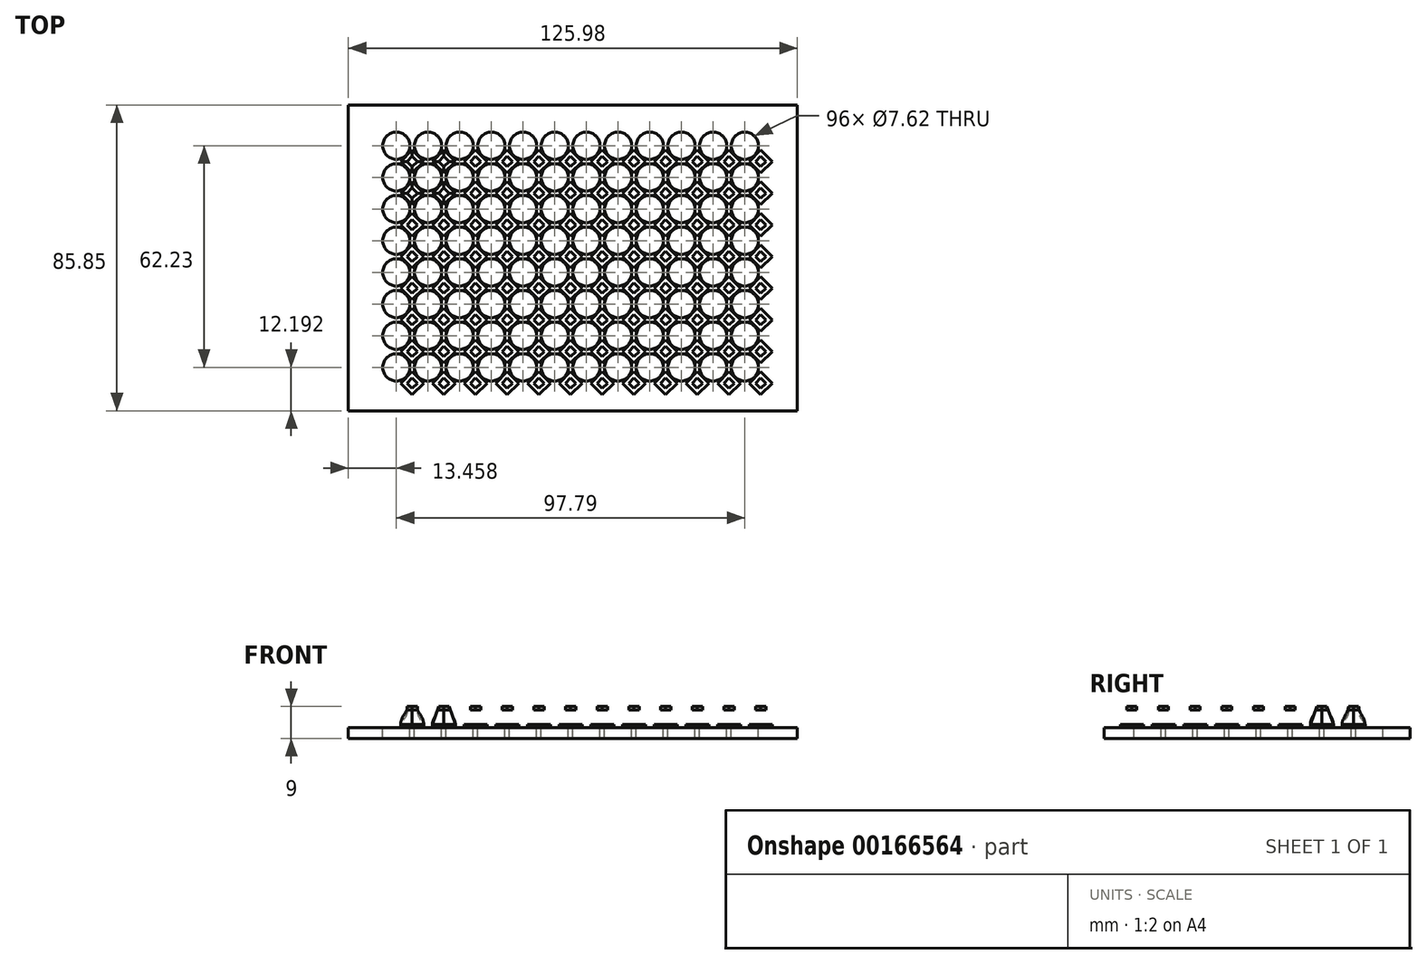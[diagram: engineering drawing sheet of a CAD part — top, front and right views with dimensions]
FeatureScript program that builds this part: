
annotation { "Feature Type Name" : "Feature", "Feature Type Description" : "" }
export const myFeature = defineFeature(function(context is Context, id is Id, definition is map)
    precondition{}
    {
        {
            var Q0;
            Q0=qCreatedBy(makeId("Top.planeOp"),FACE);
            var sketch = newSketch(context, id + "F0", { "sketchPlane" : qUnion([Q0])});
            skLineSegment(sketch, "E0.bottom", {"start": v(0, 0) * mm, "end": v(-125.98, 0) * mm});
            skLineSegment(sketch, "E0.top", {"start": v(0, 85.85) * mm, "end": v(-125.98, 85.85) * mm});
            skLineSegment(sketch, "E0.left", {"start": v(0, 0) * mm, "end": v(0, 85.85) * mm});
            skLineSegment(sketch, "E0.right", {"start": v(-125.98, 0) * mm, "end": v(-125.98, 85.85) * mm});
            skCircle(sketch, "E1", {"center": v(-112.52, 74.42) * mm, "radius": 3.81 * mm});
            skCircle(sketch, "E2.0.1.0", {"center": v(-112.52, 65.53) * mm, "radius": 3.81 * mm});
            skCircle(sketch, "E2.0.2.0", {"center": v(-112.52, 56.64) * mm, "radius": 3.81 * mm});
            skCircle(sketch, "E2.0.3.0", {"center": v(-112.52, 47.75) * mm, "radius": 3.81 * mm});
            skCircle(sketch, "E2.0.4.0", {"center": v(-112.52, 38.86) * mm, "radius": 3.81 * mm});
            skCircle(sketch, "E2.0.5.0", {"center": v(-112.52, 29.97) * mm, "radius": 3.81 * mm});
            skCircle(sketch, "E2.0.6.0", {"center": v(-112.52, 21.08) * mm, "radius": 3.81 * mm});
            skCircle(sketch, "E2.0.7.0", {"center": v(-112.52, 12.2) * mm, "radius": 3.81 * mm});
            skCircle(sketch, "E2.1.0.0", {"center": v(-103.63, 74.42) * mm, "radius": 3.81 * mm});
            skCircle(sketch, "E2.1.1.0", {"center": v(-103.63, 65.53) * mm, "radius": 3.81 * mm});
            skCircle(sketch, "E2.1.2.0", {"center": v(-103.63, 56.64) * mm, "radius": 3.81 * mm});
            skCircle(sketch, "E2.1.3.0", {"center": v(-103.63, 47.75) * mm, "radius": 3.81 * mm});
            skCircle(sketch, "E2.1.4.0", {"center": v(-103.63, 38.86) * mm, "radius": 3.81 * mm});
            skCircle(sketch, "E2.1.5.0", {"center": v(-103.63, 29.97) * mm, "radius": 3.81 * mm});
            skCircle(sketch, "E2.1.6.0", {"center": v(-103.63, 21.08) * mm, "radius": 3.81 * mm});
            skCircle(sketch, "E2.1.7.0", {"center": v(-103.63, 12.2) * mm, "radius": 3.81 * mm});
            skCircle(sketch, "E2.2.0.0", {"center": v(-94.74, 74.42) * mm, "radius": 3.81 * mm});
            skCircle(sketch, "E2.2.1.0", {"center": v(-94.74, 65.53) * mm, "radius": 3.81 * mm});
            skCircle(sketch, "E2.2.2.0", {"center": v(-94.74, 56.64) * mm, "radius": 3.81 * mm});
            skCircle(sketch, "E2.2.3.0", {"center": v(-94.74, 47.75) * mm, "radius": 3.81 * mm});
            skCircle(sketch, "E2.2.4.0", {"center": v(-94.74, 38.86) * mm, "radius": 3.81 * mm});
            skCircle(sketch, "E2.2.5.0", {"center": v(-94.74, 29.97) * mm, "radius": 3.81 * mm});
            skCircle(sketch, "E2.2.6.0", {"center": v(-94.74, 21.08) * mm, "radius": 3.81 * mm});
            skCircle(sketch, "E2.2.7.0", {"center": v(-94.74, 12.2) * mm, "radius": 3.81 * mm});
            skCircle(sketch, "E2.3.0.0", {"center": v(-85.85, 74.42) * mm, "radius": 3.81 * mm});
            skCircle(sketch, "E2.3.1.0", {"center": v(-85.85, 65.53) * mm, "radius": 3.81 * mm});
            skCircle(sketch, "E2.3.2.0", {"center": v(-85.85, 56.64) * mm, "radius": 3.81 * mm});
            skCircle(sketch, "E2.3.3.0", {"center": v(-85.85, 47.75) * mm, "radius": 3.81 * mm});
            skCircle(sketch, "E2.3.4.0", {"center": v(-85.85, 38.86) * mm, "radius": 3.81 * mm});
            skCircle(sketch, "E2.3.5.0", {"center": v(-85.85, 29.97) * mm, "radius": 3.81 * mm});
            skCircle(sketch, "E2.3.6.0", {"center": v(-85.85, 21.08) * mm, "radius": 3.81 * mm});
            skCircle(sketch, "E2.3.7.0", {"center": v(-85.85, 12.2) * mm, "radius": 3.81 * mm});
            skCircle(sketch, "E2.4.0.0", {"center": v(-76.96, 74.42) * mm, "radius": 3.81 * mm});
            skCircle(sketch, "E2.4.1.0", {"center": v(-76.96, 65.53) * mm, "radius": 3.81 * mm});
            skCircle(sketch, "E2.4.2.0", {"center": v(-76.96, 56.64) * mm, "radius": 3.81 * mm});
            skCircle(sketch, "E2.4.3.0", {"center": v(-76.96, 47.75) * mm, "radius": 3.81 * mm});
            skCircle(sketch, "E2.4.4.0", {"center": v(-76.96, 38.86) * mm, "radius": 3.81 * mm});
            skCircle(sketch, "E2.4.5.0", {"center": v(-76.96, 29.97) * mm, "radius": 3.81 * mm});
            skCircle(sketch, "E2.4.6.0", {"center": v(-76.96, 21.08) * mm, "radius": 3.81 * mm});
            skCircle(sketch, "E2.4.7.0", {"center": v(-76.96, 12.2) * mm, "radius": 3.81 * mm});
            skCircle(sketch, "E2.5.0.0", {"center": v(-68.07, 74.42) * mm, "radius": 3.81 * mm});
            skCircle(sketch, "E2.5.1.0", {"center": v(-68.07, 65.53) * mm, "radius": 3.81 * mm});
            skCircle(sketch, "E2.5.2.0", {"center": v(-68.07, 56.64) * mm, "radius": 3.81 * mm});
            skCircle(sketch, "E2.5.3.0", {"center": v(-68.07, 47.75) * mm, "radius": 3.81 * mm});
            skCircle(sketch, "E2.5.4.0", {"center": v(-68.07, 38.86) * mm, "radius": 3.81 * mm});
            skCircle(sketch, "E2.5.5.0", {"center": v(-68.07, 29.97) * mm, "radius": 3.81 * mm});
            skCircle(sketch, "E2.5.6.0", {"center": v(-68.07, 21.08) * mm, "radius": 3.81 * mm});
            skCircle(sketch, "E2.5.7.0", {"center": v(-68.07, 12.2) * mm, "radius": 3.81 * mm});
            skCircle(sketch, "E2.6.0.0", {"center": v(-59.18, 74.42) * mm, "radius": 3.81 * mm});
            skCircle(sketch, "E2.6.1.0", {"center": v(-59.18, 65.53) * mm, "radius": 3.81 * mm});
            skCircle(sketch, "E2.6.2.0", {"center": v(-59.18, 56.64) * mm, "radius": 3.81 * mm});
            skCircle(sketch, "E2.6.3.0", {"center": v(-59.18, 47.75) * mm, "radius": 3.81 * mm});
            skCircle(sketch, "E2.6.4.0", {"center": v(-59.18, 38.86) * mm, "radius": 3.81 * mm});
            skCircle(sketch, "E2.6.5.0", {"center": v(-59.18, 29.97) * mm, "radius": 3.81 * mm});
            skCircle(sketch, "E2.6.6.0", {"center": v(-59.18, 21.08) * mm, "radius": 3.81 * mm});
            skCircle(sketch, "E2.6.7.0", {"center": v(-59.18, 12.2) * mm, "radius": 3.81 * mm});
            skCircle(sketch, "E2.7.0.0", {"center": v(-50.3, 74.42) * mm, "radius": 3.81 * mm});
            skCircle(sketch, "E2.7.1.0", {"center": v(-50.3, 65.53) * mm, "radius": 3.81 * mm});
            skCircle(sketch, "E2.7.2.0", {"center": v(-50.3, 56.64) * mm, "radius": 3.81 * mm});
            skCircle(sketch, "E2.7.3.0", {"center": v(-50.3, 47.75) * mm, "radius": 3.81 * mm});
            skCircle(sketch, "E2.7.4.0", {"center": v(-50.3, 38.86) * mm, "radius": 3.81 * mm});
            skCircle(sketch, "E2.7.5.0", {"center": v(-50.3, 29.97) * mm, "radius": 3.81 * mm});
            skCircle(sketch, "E2.7.6.0", {"center": v(-50.3, 21.08) * mm, "radius": 3.81 * mm});
            skCircle(sketch, "E2.7.7.0", {"center": v(-50.3, 12.2) * mm, "radius": 3.81 * mm});
            skCircle(sketch, "E2.8.0.0", {"center": v(-41.4, 74.42) * mm, "radius": 3.81 * mm});
            skCircle(sketch, "E2.8.1.0", {"center": v(-41.4, 65.53) * mm, "radius": 3.81 * mm});
            skCircle(sketch, "E2.8.2.0", {"center": v(-41.4, 56.64) * mm, "radius": 3.81 * mm});
            skCircle(sketch, "E2.8.3.0", {"center": v(-41.4, 47.75) * mm, "radius": 3.81 * mm});
            skCircle(sketch, "E2.8.4.0", {"center": v(-41.4, 38.86) * mm, "radius": 3.81 * mm});
            skCircle(sketch, "E2.8.5.0", {"center": v(-41.4, 29.97) * mm, "radius": 3.81 * mm});
            skCircle(sketch, "E2.8.6.0", {"center": v(-41.4, 21.08) * mm, "radius": 3.81 * mm});
            skCircle(sketch, "E2.8.7.0", {"center": v(-41.4, 12.2) * mm, "radius": 3.81 * mm});
            skCircle(sketch, "E2.9.0.0", {"center": v(-32.51, 74.42) * mm, "radius": 3.81 * mm});
            skCircle(sketch, "E2.9.1.0", {"center": v(-32.51, 65.53) * mm, "radius": 3.81 * mm});
            skCircle(sketch, "E2.9.2.0", {"center": v(-32.51, 56.64) * mm, "radius": 3.81 * mm});
            skCircle(sketch, "E2.9.3.0", {"center": v(-32.51, 47.75) * mm, "radius": 3.81 * mm});
            skCircle(sketch, "E2.9.4.0", {"center": v(-32.51, 38.86) * mm, "radius": 3.81 * mm});
            skCircle(sketch, "E2.9.5.0", {"center": v(-32.51, 29.97) * mm, "radius": 3.81 * mm});
            skCircle(sketch, "E2.9.6.0", {"center": v(-32.51, 21.08) * mm, "radius": 3.81 * mm});
            skCircle(sketch, "E2.9.7.0", {"center": v(-32.51, 12.2) * mm, "radius": 3.81 * mm});
            skCircle(sketch, "E2.10.0.0", {"center": v(-23.62, 74.42) * mm, "radius": 3.81 * mm});
            skCircle(sketch, "E2.10.1.0", {"center": v(-23.62, 65.53) * mm, "radius": 3.81 * mm});
            skCircle(sketch, "E2.10.2.0", {"center": v(-23.62, 56.64) * mm, "radius": 3.81 * mm});
            skCircle(sketch, "E2.10.3.0", {"center": v(-23.62, 47.75) * mm, "radius": 3.81 * mm});
            skCircle(sketch, "E2.10.4.0", {"center": v(-23.62, 38.86) * mm, "radius": 3.81 * mm});
            skCircle(sketch, "E2.10.5.0", {"center": v(-23.62, 29.97) * mm, "radius": 3.81 * mm});
            skCircle(sketch, "E2.10.6.0", {"center": v(-23.62, 21.08) * mm, "radius": 3.81 * mm});
            skCircle(sketch, "E2.10.7.0", {"center": v(-23.62, 12.2) * mm, "radius": 3.81 * mm});
            skCircle(sketch, "E2.11.0.0", {"center": v(-14.73, 74.42) * mm, "radius": 3.81 * mm});
            skCircle(sketch, "E2.11.1.0", {"center": v(-14.73, 65.53) * mm, "radius": 3.81 * mm});
            skCircle(sketch, "E2.11.2.0", {"center": v(-14.73, 56.64) * mm, "radius": 3.81 * mm});
            skCircle(sketch, "E2.11.3.0", {"center": v(-14.73, 47.75) * mm, "radius": 3.81 * mm});
            skCircle(sketch, "E2.11.4.0", {"center": v(-14.73, 38.86) * mm, "radius": 3.81 * mm});
            skCircle(sketch, "E2.11.5.0", {"center": v(-14.73, 29.97) * mm, "radius": 3.81 * mm});
            skCircle(sketch, "E2.11.6.0", {"center": v(-14.73, 21.08) * mm, "radius": 3.81 * mm});
            skCircle(sketch, "E2.11.7.0", {"center": v(-14.73, 12.2) * mm, "radius": 3.81 * mm});
            skLineSegment(sketch, "E2.direction1", {"start": v(-112.52, 74.42) * mm, "end": v(-103.63, 74.42) * mm, "construction": true});
            skLineSegment(sketch, "E2.direction2", {"start": v(-112.52, 74.42) * mm, "end": v(-112.52, 65.53) * mm, "construction": true});
            skPoint(sketch, "E3", {"position": v(-112.52, 78.23) * mm});
            skPoint(sketch, "E4", {"position": v(-115.74, 72.39) * mm});
            skPoint(sketch, "E5", {"position": v(-109.3, 72.39) * mm});
            skSolve(sketch);
        }
        {
            var Q0;
            Q0=makeQuery(id+"F0.imprint","IMPRINT",FACE,{"disambiguationData":[TD([[makeQuery(id+"F0.imprint","IMPRINT",EDGE,{"derivedFrom":sQuery(id+"F0.wireOp",EDGE,"E0.bottom")}),-1.0]])]});
            extrude(context, id + "F1", {"entities" : qUnion([Q0]), "oppositeDirection" : true, "depth" : 3 * mm});
        }
        {
            var Q0;
            Q0=makeQuery(id+"F1.opExtrude","CAP_FACE",FACE,{"disambiguationData":[OSD([sQuery(id+"F0.wireOp",EDGE,"E0.bottom"),sQuery(id+"F0.wireOp",EDGE,"E0.top"),sQuery(id+"F0.wireOp",EDGE,"E0.left"),sQuery(id+"F0.wireOp",EDGE,"E0.right"),sQuery(id+"F0.wireOp",EDGE,"E1"),sQuery(id+"F0.wireOp",EDGE,"E2.0.1.0"),sQuery(id+"F0.wireOp",EDGE,"E2.0.2.0"),sQuery(id+"F0.wireOp",EDGE,"E2.0.3.0"),sQuery(id+"F0.wireOp",EDGE,"E2.0.4.0"),sQuery(id+"F0.wireOp",EDGE,"E2.0.5.0"),sQuery(id+"F0.wireOp",EDGE,"E2.0.6.0"),sQuery(id+"F0.wireOp",EDGE,"E2.0.7.0"),sQuery(id+"F0.wireOp",EDGE,"E2.1.0.0"),sQuery(id+"F0.wireOp",EDGE,"E2.1.1.0"),sQuery(id+"F0.wireOp",EDGE,"E2.1.2.0"),sQuery(id+"F0.wireOp",EDGE,"E2.1.3.0"),sQuery(id+"F0.wireOp",EDGE,"E2.1.4.0"),sQuery(id+"F0.wireOp",EDGE,"E2.1.5.0"),sQuery(id+"F0.wireOp",EDGE,"E2.1.6.0"),sQuery(id+"F0.wireOp",EDGE,"E2.1.7.0"),sQuery(id+"F0.wireOp",EDGE,"E2.2.0.0"),sQuery(id+"F0.wireOp",EDGE,"E2.2.1.0"),sQuery(id+"F0.wireOp",EDGE,"E2.2.2.0"),sQuery(id+"F0.wireOp",EDGE,"E2.2.3.0"),sQuery(id+"F0.wireOp",EDGE,"E2.2.4.0"),sQuery(id+"F0.wireOp",EDGE,"E2.2.5.0"),sQuery(id+"F0.wireOp",EDGE,"E2.2.6.0"),sQuery(id+"F0.wireOp",EDGE,"E2.2.7.0"),sQuery(id+"F0.wireOp",EDGE,"E2.3.0.0"),sQuery(id+"F0.wireOp",EDGE,"E2.3.1.0"),sQuery(id+"F0.wireOp",EDGE,"E2.3.2.0"),sQuery(id+"F0.wireOp",EDGE,"E2.3.3.0"),sQuery(id+"F0.wireOp",EDGE,"E2.3.4.0"),sQuery(id+"F0.wireOp",EDGE,"E2.3.5.0"),sQuery(id+"F0.wireOp",EDGE,"E2.3.6.0"),sQuery(id+"F0.wireOp",EDGE,"E2.3.7.0"),sQuery(id+"F0.wireOp",EDGE,"E2.4.0.0"),sQuery(id+"F0.wireOp",EDGE,"E2.4.1.0"),sQuery(id+"F0.wireOp",EDGE,"E2.4.2.0"),sQuery(id+"F0.wireOp",EDGE,"E2.4.3.0"),sQuery(id+"F0.wireOp",EDGE,"E2.4.4.0"),sQuery(id+"F0.wireOp",EDGE,"E2.4.5.0"),sQuery(id+"F0.wireOp",EDGE,"E2.4.6.0"),sQuery(id+"F0.wireOp",EDGE,"E2.4.7.0"),sQuery(id+"F0.wireOp",EDGE,"E2.5.0.0"),sQuery(id+"F0.wireOp",EDGE,"E2.5.1.0"),sQuery(id+"F0.wireOp",EDGE,"E2.5.2.0"),sQuery(id+"F0.wireOp",EDGE,"E2.5.3.0"),sQuery(id+"F0.wireOp",EDGE,"E2.5.4.0"),sQuery(id+"F0.wireOp",EDGE,"E2.5.5.0"),sQuery(id+"F0.wireOp",EDGE,"E2.5.6.0"),sQuery(id+"F0.wireOp",EDGE,"E2.5.7.0"),sQuery(id+"F0.wireOp",EDGE,"E2.6.0.0"),sQuery(id+"F0.wireOp",EDGE,"E2.6.1.0"),sQuery(id+"F0.wireOp",EDGE,"E2.6.2.0"),sQuery(id+"F0.wireOp",EDGE,"E2.6.3.0"),sQuery(id+"F0.wireOp",EDGE,"E2.6.4.0"),sQuery(id+"F0.wireOp",EDGE,"E2.6.5.0"),sQuery(id+"F0.wireOp",EDGE,"E2.6.6.0"),sQuery(id+"F0.wireOp",EDGE,"E2.6.7.0"),sQuery(id+"F0.wireOp",EDGE,"E2.7.0.0"),sQuery(id+"F0.wireOp",EDGE,"E2.7.1.0"),sQuery(id+"F0.wireOp",EDGE,"E2.7.2.0"),sQuery(id+"F0.wireOp",EDGE,"E2.7.3.0"),sQuery(id+"F0.wireOp",EDGE,"E2.7.4.0"),sQuery(id+"F0.wireOp",EDGE,"E2.7.5.0"),sQuery(id+"F0.wireOp",EDGE,"E2.7.6.0"),sQuery(id+"F0.wireOp",EDGE,"E2.7.7.0"),sQuery(id+"F0.wireOp",EDGE,"E2.8.0.0"),sQuery(id+"F0.wireOp",EDGE,"E2.8.1.0"),sQuery(id+"F0.wireOp",EDGE,"E2.8.2.0"),sQuery(id+"F0.wireOp",EDGE,"E2.8.3.0"),sQuery(id+"F0.wireOp",EDGE,"E2.8.4.0"),sQuery(id+"F0.wireOp",EDGE,"E2.8.5.0"),sQuery(id+"F0.wireOp",EDGE,"E2.8.6.0"),sQuery(id+"F0.wireOp",EDGE,"E2.8.7.0"),sQuery(id+"F0.wireOp",EDGE,"E2.9.0.0"),sQuery(id+"F0.wireOp",EDGE,"E2.9.1.0"),sQuery(id+"F0.wireOp",EDGE,"E2.9.2.0"),sQuery(id+"F0.wireOp",EDGE,"E2.9.3.0"),sQuery(id+"F0.wireOp",EDGE,"E2.9.4.0"),sQuery(id+"F0.wireOp",EDGE,"E2.9.5.0"),sQuery(id+"F0.wireOp",EDGE,"E2.9.6.0"),sQuery(id+"F0.wireOp",EDGE,"E2.9.7.0"),sQuery(id+"F0.wireOp",EDGE,"E2.10.0.0"),sQuery(id+"F0.wireOp",EDGE,"E2.10.1.0"),sQuery(id+"F0.wireOp",EDGE,"E2.10.2.0"),sQuery(id+"F0.wireOp",EDGE,"E2.10.3.0"),sQuery(id+"F0.wireOp",EDGE,"E2.10.4.0"),sQuery(id+"F0.wireOp",EDGE,"E2.10.5.0"),sQuery(id+"F0.wireOp",EDGE,"E2.10.6.0"),sQuery(id+"F0.wireOp",EDGE,"E2.10.7.0"),sQuery(id+"F0.wireOp",EDGE,"E2.11.0.0"),sQuery(id+"F0.wireOp",EDGE,"E2.11.1.0"),sQuery(id+"F0.wireOp",EDGE,"E2.11.2.0"),sQuery(id+"F0.wireOp",EDGE,"E2.11.3.0"),sQuery(id+"F0.wireOp",EDGE,"E2.11.4.0"),sQuery(id+"F0.wireOp",EDGE,"E2.11.5.0"),sQuery(id+"F0.wireOp",EDGE,"E2.11.6.0"),sQuery(id+"F0.wireOp",EDGE,"E2.11.7.0")])],"isStart":false});
            var sketch = newSketch(context, id + "F2", { "sketchPlane" : qUnion([Q0])});
            skLineSegment(sketch, "E6", {"start": v(-108.08, -73.2) * mm, "end": v(-104.84, -69.98) * mm});
            skLineSegment(sketch, "E7", {"start": v(-104.84, -69.98) * mm, "end": v(-108.08, -66.74) * mm});
            skLineSegment(sketch, "E8", {"start": v(-108.08, -66.74) * mm, "end": v(-111.3, -69.98) * mm});
            skLineSegment(sketch, "E9", {"start": v(-111.3, -69.98) * mm, "end": v(-108.08, -73.2) * mm});
            skLineSegment(sketch, "E10", {"start": v(-112.52, -74.42) * mm, "end": v(-103.63, -74.42) * mm, "construction": true});
            skLineSegment(sketch, "E11", {"start": v(-112.52, -65.53) * mm, "end": v(-112.52, -74.42) * mm, "construction": true});
            skPoint(sketch, "E12", {"position": v(-108.08, -74.42) * mm});
            skPoint(sketch, "E13", {"position": v(-112.52, -69.98) * mm});
            skLineSegment(sketch, "E14.0.1.0", {"start": v(-108.08, -57.85) * mm, "end": v(-111.3, -61.09) * mm});
            skLineSegment(sketch, "E14.0.1.1", {"start": v(-111.3, -61.09) * mm, "end": v(-108.08, -64.32) * mm});
            skLineSegment(sketch, "E14.0.1.2", {"start": v(-108.08, -64.32) * mm, "end": v(-104.84, -61.09) * mm});
            skLineSegment(sketch, "E14.0.1.3", {"start": v(-104.84, -61.09) * mm, "end": v(-108.08, -57.85) * mm});
            skLineSegment(sketch, "E14.0.2.0", {"start": v(-108.08, -48.96) * mm, "end": v(-111.3, -52.2) * mm});
            skLineSegment(sketch, "E14.0.2.1", {"start": v(-111.3, -52.2) * mm, "end": v(-108.08, -55.43) * mm});
            skLineSegment(sketch, "E14.0.2.2", {"start": v(-108.08, -55.43) * mm, "end": v(-104.84, -52.2) * mm});
            skLineSegment(sketch, "E14.0.2.3", {"start": v(-104.84, -52.2) * mm, "end": v(-108.08, -48.96) * mm});
            skLineSegment(sketch, "E14.0.3.0", {"start": v(-108.08, -40.07) * mm, "end": v(-111.3, -43.3) * mm});
            skLineSegment(sketch, "E14.0.3.1", {"start": v(-111.3, -43.3) * mm, "end": v(-108.08, -46.54) * mm});
            skLineSegment(sketch, "E14.0.3.2", {"start": v(-108.08, -46.54) * mm, "end": v(-104.84, -43.3) * mm});
            skLineSegment(sketch, "E14.0.3.3", {"start": v(-104.84, -43.3) * mm, "end": v(-108.08, -40.07) * mm});
            skLineSegment(sketch, "E14.0.4.0", {"start": v(-108.08, -31.18) * mm, "end": v(-111.3, -34.42) * mm});
            skLineSegment(sketch, "E14.0.4.1", {"start": v(-111.3, -34.42) * mm, "end": v(-108.08, -37.65) * mm});
            skLineSegment(sketch, "E14.0.4.2", {"start": v(-108.08, -37.65) * mm, "end": v(-104.84, -34.42) * mm});
            skLineSegment(sketch, "E14.0.4.3", {"start": v(-104.84, -34.42) * mm, "end": v(-108.08, -31.18) * mm});
            skLineSegment(sketch, "E14.0.5.0", {"start": v(-108.08, -22.3) * mm, "end": v(-111.3, -25.53) * mm});
            skLineSegment(sketch, "E14.0.5.1", {"start": v(-111.3, -25.53) * mm, "end": v(-108.08, -28.76) * mm});
            skLineSegment(sketch, "E14.0.5.2", {"start": v(-108.08, -28.76) * mm, "end": v(-104.84, -25.53) * mm});
            skLineSegment(sketch, "E14.0.5.3", {"start": v(-104.84, -25.53) * mm, "end": v(-108.08, -22.3) * mm});
            skLineSegment(sketch, "E14.0.6.0", {"start": v(-108.08, -13.4) * mm, "end": v(-111.3, -16.64) * mm});
            skLineSegment(sketch, "E14.0.6.1", {"start": v(-111.3, -16.64) * mm, "end": v(-108.08, -19.87) * mm});
            skLineSegment(sketch, "E14.0.6.2", {"start": v(-108.08, -19.87) * mm, "end": v(-104.84, -16.64) * mm});
            skLineSegment(sketch, "E14.0.6.3", {"start": v(-104.84, -16.64) * mm, "end": v(-108.08, -13.4) * mm});
            skLineSegment(sketch, "E14.0.7.0", {"start": v(-108.08, -4.51) * mm, "end": v(-111.3, -7.75) * mm});
            skLineSegment(sketch, "E14.0.7.1", {"start": v(-111.3, -7.75) * mm, "end": v(-108.08, -10.98) * mm});
            skLineSegment(sketch, "E14.0.7.2", {"start": v(-108.08, -10.98) * mm, "end": v(-104.84, -7.75) * mm});
            skLineSegment(sketch, "E14.0.7.3", {"start": v(-104.84, -7.75) * mm, "end": v(-108.08, -4.51) * mm});
            skLineSegment(sketch, "E14.1.0.0", {"start": v(-99.19, -66.74) * mm, "end": v(-102.42, -69.98) * mm});
            skLineSegment(sketch, "E14.1.0.1", {"start": v(-102.42, -69.98) * mm, "end": v(-99.19, -73.2) * mm});
            skLineSegment(sketch, "E14.1.0.2", {"start": v(-99.19, -73.2) * mm, "end": v(-95.95, -69.98) * mm});
            skLineSegment(sketch, "E14.1.0.3", {"start": v(-95.95, -69.98) * mm, "end": v(-99.19, -66.74) * mm});
            skLineSegment(sketch, "E14.1.1.0", {"start": v(-99.19, -57.85) * mm, "end": v(-102.42, -61.09) * mm});
            skLineSegment(sketch, "E14.1.1.1", {"start": v(-102.42, -61.09) * mm, "end": v(-99.19, -64.32) * mm});
            skLineSegment(sketch, "E14.1.1.2", {"start": v(-99.19, -64.32) * mm, "end": v(-95.95, -61.09) * mm});
            skLineSegment(sketch, "E14.1.1.3", {"start": v(-95.95, -61.09) * mm, "end": v(-99.19, -57.85) * mm});
            skLineSegment(sketch, "E14.1.2.0", {"start": v(-99.19, -48.96) * mm, "end": v(-102.42, -52.2) * mm});
            skLineSegment(sketch, "E14.1.2.1", {"start": v(-102.42, -52.2) * mm, "end": v(-99.19, -55.43) * mm});
            skLineSegment(sketch, "E14.1.2.2", {"start": v(-99.19, -55.43) * mm, "end": v(-95.95, -52.2) * mm});
            skLineSegment(sketch, "E14.1.2.3", {"start": v(-95.95, -52.2) * mm, "end": v(-99.19, -48.96) * mm});
            skLineSegment(sketch, "E14.1.3.0", {"start": v(-99.19, -40.07) * mm, "end": v(-102.42, -43.3) * mm});
            skLineSegment(sketch, "E14.1.3.1", {"start": v(-102.42, -43.3) * mm, "end": v(-99.19, -46.54) * mm});
            skLineSegment(sketch, "E14.1.3.2", {"start": v(-99.19, -46.54) * mm, "end": v(-95.95, -43.3) * mm});
            skLineSegment(sketch, "E14.1.3.3", {"start": v(-95.95, -43.3) * mm, "end": v(-99.19, -40.07) * mm});
            skLineSegment(sketch, "E14.1.4.0", {"start": v(-99.19, -31.18) * mm, "end": v(-102.42, -34.42) * mm});
            skLineSegment(sketch, "E14.1.4.1", {"start": v(-102.42, -34.42) * mm, "end": v(-99.19, -37.65) * mm});
            skLineSegment(sketch, "E14.1.4.2", {"start": v(-99.19, -37.65) * mm, "end": v(-95.95, -34.42) * mm});
            skLineSegment(sketch, "E14.1.4.3", {"start": v(-95.95, -34.42) * mm, "end": v(-99.19, -31.18) * mm});
            skLineSegment(sketch, "E14.1.5.0", {"start": v(-99.19, -22.3) * mm, "end": v(-102.42, -25.53) * mm});
            skLineSegment(sketch, "E14.1.5.1", {"start": v(-102.42, -25.53) * mm, "end": v(-99.19, -28.76) * mm});
            skLineSegment(sketch, "E14.1.5.2", {"start": v(-99.19, -28.76) * mm, "end": v(-95.95, -25.53) * mm});
            skLineSegment(sketch, "E14.1.5.3", {"start": v(-95.95, -25.53) * mm, "end": v(-99.19, -22.3) * mm});
            skLineSegment(sketch, "E14.1.6.0", {"start": v(-99.19, -13.4) * mm, "end": v(-102.42, -16.64) * mm});
            skLineSegment(sketch, "E14.1.6.1", {"start": v(-102.42, -16.64) * mm, "end": v(-99.19, -19.87) * mm});
            skLineSegment(sketch, "E14.1.6.2", {"start": v(-99.19, -19.87) * mm, "end": v(-95.95, -16.64) * mm});
            skLineSegment(sketch, "E14.1.6.3", {"start": v(-95.95, -16.64) * mm, "end": v(-99.19, -13.4) * mm});
            skLineSegment(sketch, "E14.1.7.0", {"start": v(-99.19, -4.51) * mm, "end": v(-102.42, -7.75) * mm});
            skLineSegment(sketch, "E14.1.7.1", {"start": v(-102.42, -7.75) * mm, "end": v(-99.19, -10.98) * mm});
            skLineSegment(sketch, "E14.1.7.2", {"start": v(-99.19, -10.98) * mm, "end": v(-95.95, -7.75) * mm});
            skLineSegment(sketch, "E14.1.7.3", {"start": v(-95.95, -7.75) * mm, "end": v(-99.19, -4.51) * mm});
            skLineSegment(sketch, "E14.2.0.0", {"start": v(-90.3, -66.74) * mm, "end": v(-93.53, -69.98) * mm});
            skLineSegment(sketch, "E14.2.0.1", {"start": v(-93.53, -69.98) * mm, "end": v(-90.3, -73.2) * mm});
            skLineSegment(sketch, "E14.2.0.2", {"start": v(-90.3, -73.2) * mm, "end": v(-87.06, -69.98) * mm});
            skLineSegment(sketch, "E14.2.0.3", {"start": v(-87.06, -69.98) * mm, "end": v(-90.3, -66.74) * mm});
            skLineSegment(sketch, "E14.2.1.0", {"start": v(-90.3, -57.85) * mm, "end": v(-93.53, -61.09) * mm});
            skLineSegment(sketch, "E14.2.1.1", {"start": v(-93.53, -61.09) * mm, "end": v(-90.3, -64.32) * mm});
            skLineSegment(sketch, "E14.2.1.2", {"start": v(-90.3, -64.32) * mm, "end": v(-87.06, -61.09) * mm});
            skLineSegment(sketch, "E14.2.1.3", {"start": v(-87.06, -61.09) * mm, "end": v(-90.3, -57.85) * mm});
            skLineSegment(sketch, "E14.2.2.0", {"start": v(-90.3, -48.96) * mm, "end": v(-93.53, -52.2) * mm});
            skLineSegment(sketch, "E14.2.2.1", {"start": v(-93.53, -52.2) * mm, "end": v(-90.3, -55.43) * mm});
            skLineSegment(sketch, "E14.2.2.2", {"start": v(-90.3, -55.43) * mm, "end": v(-87.06, -52.2) * mm});
            skLineSegment(sketch, "E14.2.2.3", {"start": v(-87.06, -52.2) * mm, "end": v(-90.3, -48.96) * mm});
            skLineSegment(sketch, "E14.2.3.0", {"start": v(-90.3, -40.07) * mm, "end": v(-93.53, -43.3) * mm});
            skLineSegment(sketch, "E14.2.3.1", {"start": v(-93.53, -43.3) * mm, "end": v(-90.3, -46.54) * mm});
            skLineSegment(sketch, "E14.2.3.2", {"start": v(-90.3, -46.54) * mm, "end": v(-87.06, -43.3) * mm});
            skLineSegment(sketch, "E14.2.3.3", {"start": v(-87.06, -43.3) * mm, "end": v(-90.3, -40.07) * mm});
            skLineSegment(sketch, "E14.2.4.0", {"start": v(-90.3, -31.18) * mm, "end": v(-93.53, -34.42) * mm});
            skLineSegment(sketch, "E14.2.4.1", {"start": v(-93.53, -34.42) * mm, "end": v(-90.3, -37.65) * mm});
            skLineSegment(sketch, "E14.2.4.2", {"start": v(-90.3, -37.65) * mm, "end": v(-87.06, -34.42) * mm});
            skLineSegment(sketch, "E14.2.4.3", {"start": v(-87.06, -34.42) * mm, "end": v(-90.3, -31.18) * mm});
            skLineSegment(sketch, "E14.2.5.0", {"start": v(-90.3, -22.3) * mm, "end": v(-93.53, -25.53) * mm});
            skLineSegment(sketch, "E14.2.5.1", {"start": v(-93.53, -25.53) * mm, "end": v(-90.3, -28.76) * mm});
            skLineSegment(sketch, "E14.2.5.2", {"start": v(-90.3, -28.76) * mm, "end": v(-87.06, -25.53) * mm});
            skLineSegment(sketch, "E14.2.5.3", {"start": v(-87.06, -25.53) * mm, "end": v(-90.3, -22.3) * mm});
            skLineSegment(sketch, "E14.2.6.0", {"start": v(-90.3, -13.4) * mm, "end": v(-93.53, -16.64) * mm});
            skLineSegment(sketch, "E14.2.6.1", {"start": v(-93.53, -16.64) * mm, "end": v(-90.3, -19.87) * mm});
            skLineSegment(sketch, "E14.2.6.2", {"start": v(-90.3, -19.87) * mm, "end": v(-87.06, -16.64) * mm});
            skLineSegment(sketch, "E14.2.6.3", {"start": v(-87.06, -16.64) * mm, "end": v(-90.3, -13.4) * mm});
            skLineSegment(sketch, "E14.2.7.0", {"start": v(-90.3, -4.51) * mm, "end": v(-93.53, -7.75) * mm});
            skLineSegment(sketch, "E14.2.7.1", {"start": v(-93.53, -7.75) * mm, "end": v(-90.3, -10.98) * mm});
            skLineSegment(sketch, "E14.2.7.2", {"start": v(-90.3, -10.98) * mm, "end": v(-87.06, -7.75) * mm});
            skLineSegment(sketch, "E14.2.7.3", {"start": v(-87.06, -7.75) * mm, "end": v(-90.3, -4.51) * mm});
            skLineSegment(sketch, "E14.3.0.0", {"start": v(-81.4, -66.74) * mm, "end": v(-84.64, -69.98) * mm});
            skLineSegment(sketch, "E14.3.0.1", {"start": v(-84.64, -69.98) * mm, "end": v(-81.4, -73.2) * mm});
            skLineSegment(sketch, "E14.3.0.2", {"start": v(-81.4, -73.2) * mm, "end": v(-78.17, -69.98) * mm});
            skLineSegment(sketch, "E14.3.0.3", {"start": v(-78.17, -69.98) * mm, "end": v(-81.4, -66.74) * mm});
            skLineSegment(sketch, "E14.3.1.0", {"start": v(-81.4, -57.85) * mm, "end": v(-84.64, -61.09) * mm});
            skLineSegment(sketch, "E14.3.1.1", {"start": v(-84.64, -61.09) * mm, "end": v(-81.4, -64.32) * mm});
            skLineSegment(sketch, "E14.3.1.2", {"start": v(-81.4, -64.32) * mm, "end": v(-78.17, -61.09) * mm});
            skLineSegment(sketch, "E14.3.1.3", {"start": v(-78.17, -61.09) * mm, "end": v(-81.4, -57.85) * mm});
            skLineSegment(sketch, "E14.3.2.0", {"start": v(-81.4, -48.96) * mm, "end": v(-84.64, -52.2) * mm});
            skLineSegment(sketch, "E14.3.2.1", {"start": v(-84.64, -52.2) * mm, "end": v(-81.4, -55.43) * mm});
            skLineSegment(sketch, "E14.3.2.2", {"start": v(-81.4, -55.43) * mm, "end": v(-78.17, -52.2) * mm});
            skLineSegment(sketch, "E14.3.2.3", {"start": v(-78.17, -52.2) * mm, "end": v(-81.4, -48.96) * mm});
            skLineSegment(sketch, "E14.3.3.0", {"start": v(-81.4, -40.07) * mm, "end": v(-84.64, -43.3) * mm});
            skLineSegment(sketch, "E14.3.3.1", {"start": v(-84.64, -43.3) * mm, "end": v(-81.4, -46.54) * mm});
            skLineSegment(sketch, "E14.3.3.2", {"start": v(-81.4, -46.54) * mm, "end": v(-78.17, -43.3) * mm});
            skLineSegment(sketch, "E14.3.3.3", {"start": v(-78.17, -43.3) * mm, "end": v(-81.4, -40.07) * mm});
            skLineSegment(sketch, "E14.3.4.0", {"start": v(-81.4, -31.18) * mm, "end": v(-84.64, -34.42) * mm});
            skLineSegment(sketch, "E14.3.4.1", {"start": v(-84.64, -34.42) * mm, "end": v(-81.4, -37.65) * mm});
            skLineSegment(sketch, "E14.3.4.2", {"start": v(-81.4, -37.65) * mm, "end": v(-78.17, -34.42) * mm});
            skLineSegment(sketch, "E14.3.4.3", {"start": v(-78.17, -34.42) * mm, "end": v(-81.4, -31.18) * mm});
            skLineSegment(sketch, "E14.3.5.0", {"start": v(-81.4, -22.3) * mm, "end": v(-84.64, -25.53) * mm});
            skLineSegment(sketch, "E14.3.5.1", {"start": v(-84.64, -25.53) * mm, "end": v(-81.4, -28.76) * mm});
            skLineSegment(sketch, "E14.3.5.2", {"start": v(-81.4, -28.76) * mm, "end": v(-78.17, -25.53) * mm});
            skLineSegment(sketch, "E14.3.5.3", {"start": v(-78.17, -25.53) * mm, "end": v(-81.4, -22.3) * mm});
            skLineSegment(sketch, "E14.3.6.0", {"start": v(-81.4, -13.4) * mm, "end": v(-84.64, -16.64) * mm});
            skLineSegment(sketch, "E14.3.6.1", {"start": v(-84.64, -16.64) * mm, "end": v(-81.4, -19.87) * mm});
            skLineSegment(sketch, "E14.3.6.2", {"start": v(-81.4, -19.87) * mm, "end": v(-78.17, -16.64) * mm});
            skLineSegment(sketch, "E14.3.6.3", {"start": v(-78.17, -16.64) * mm, "end": v(-81.4, -13.4) * mm});
            skLineSegment(sketch, "E14.3.7.0", {"start": v(-81.4, -4.51) * mm, "end": v(-84.64, -7.75) * mm});
            skLineSegment(sketch, "E14.3.7.1", {"start": v(-84.64, -7.75) * mm, "end": v(-81.4, -10.98) * mm});
            skLineSegment(sketch, "E14.3.7.2", {"start": v(-81.4, -10.98) * mm, "end": v(-78.17, -7.75) * mm});
            skLineSegment(sketch, "E14.3.7.3", {"start": v(-78.17, -7.75) * mm, "end": v(-81.4, -4.51) * mm});
            skLineSegment(sketch, "E14.4.0.0", {"start": v(-72.52, -66.74) * mm, "end": v(-75.75, -69.98) * mm});
            skLineSegment(sketch, "E14.4.0.1", {"start": v(-75.75, -69.98) * mm, "end": v(-72.52, -73.2) * mm});
            skLineSegment(sketch, "E14.4.0.2", {"start": v(-72.52, -73.2) * mm, "end": v(-69.28, -69.98) * mm});
            skLineSegment(sketch, "E14.4.0.3", {"start": v(-69.28, -69.98) * mm, "end": v(-72.52, -66.74) * mm});
            skLineSegment(sketch, "E14.4.1.0", {"start": v(-72.52, -57.85) * mm, "end": v(-75.75, -61.09) * mm});
            skLineSegment(sketch, "E14.4.1.1", {"start": v(-75.75, -61.09) * mm, "end": v(-72.52, -64.32) * mm});
            skLineSegment(sketch, "E14.4.1.2", {"start": v(-72.52, -64.32) * mm, "end": v(-69.28, -61.09) * mm});
            skLineSegment(sketch, "E14.4.1.3", {"start": v(-69.28, -61.09) * mm, "end": v(-72.52, -57.85) * mm});
            skLineSegment(sketch, "E14.4.2.0", {"start": v(-72.52, -48.96) * mm, "end": v(-75.75, -52.2) * mm});
            skLineSegment(sketch, "E14.4.2.1", {"start": v(-75.75, -52.2) * mm, "end": v(-72.52, -55.43) * mm});
            skLineSegment(sketch, "E14.4.2.2", {"start": v(-72.52, -55.43) * mm, "end": v(-69.28, -52.2) * mm});
            skLineSegment(sketch, "E14.4.2.3", {"start": v(-69.28, -52.2) * mm, "end": v(-72.52, -48.96) * mm});
            skLineSegment(sketch, "E14.4.3.0", {"start": v(-72.52, -40.07) * mm, "end": v(-75.75, -43.3) * mm});
            skLineSegment(sketch, "E14.4.3.1", {"start": v(-75.75, -43.3) * mm, "end": v(-72.52, -46.54) * mm});
            skLineSegment(sketch, "E14.4.3.2", {"start": v(-72.52, -46.54) * mm, "end": v(-69.28, -43.3) * mm});
            skLineSegment(sketch, "E14.4.3.3", {"start": v(-69.28, -43.3) * mm, "end": v(-72.52, -40.07) * mm});
            skLineSegment(sketch, "E14.4.4.0", {"start": v(-72.52, -31.18) * mm, "end": v(-75.75, -34.42) * mm});
            skLineSegment(sketch, "E14.4.4.1", {"start": v(-75.75, -34.42) * mm, "end": v(-72.52, -37.65) * mm});
            skLineSegment(sketch, "E14.4.4.2", {"start": v(-72.52, -37.65) * mm, "end": v(-69.28, -34.42) * mm});
            skLineSegment(sketch, "E14.4.4.3", {"start": v(-69.28, -34.42) * mm, "end": v(-72.52, -31.18) * mm});
            skLineSegment(sketch, "E14.4.5.0", {"start": v(-72.52, -22.3) * mm, "end": v(-75.75, -25.53) * mm});
            skLineSegment(sketch, "E14.4.5.1", {"start": v(-75.75, -25.53) * mm, "end": v(-72.52, -28.76) * mm});
            skLineSegment(sketch, "E14.4.5.2", {"start": v(-72.52, -28.76) * mm, "end": v(-69.28, -25.53) * mm});
            skLineSegment(sketch, "E14.4.5.3", {"start": v(-69.28, -25.53) * mm, "end": v(-72.52, -22.3) * mm});
            skLineSegment(sketch, "E14.4.6.0", {"start": v(-72.52, -13.4) * mm, "end": v(-75.75, -16.64) * mm});
            skLineSegment(sketch, "E14.4.6.1", {"start": v(-75.75, -16.64) * mm, "end": v(-72.52, -19.87) * mm});
            skLineSegment(sketch, "E14.4.6.2", {"start": v(-72.52, -19.87) * mm, "end": v(-69.28, -16.64) * mm});
            skLineSegment(sketch, "E14.4.6.3", {"start": v(-69.28, -16.64) * mm, "end": v(-72.52, -13.4) * mm});
            skLineSegment(sketch, "E14.4.7.0", {"start": v(-72.52, -4.51) * mm, "end": v(-75.75, -7.75) * mm});
            skLineSegment(sketch, "E14.4.7.1", {"start": v(-75.75, -7.75) * mm, "end": v(-72.52, -10.98) * mm});
            skLineSegment(sketch, "E14.4.7.2", {"start": v(-72.52, -10.98) * mm, "end": v(-69.28, -7.75) * mm});
            skLineSegment(sketch, "E14.4.7.3", {"start": v(-69.28, -7.75) * mm, "end": v(-72.52, -4.51) * mm});
            skLineSegment(sketch, "E14.5.0.0", {"start": v(-63.63, -66.74) * mm, "end": v(-66.86, -69.98) * mm});
            skLineSegment(sketch, "E14.5.0.1", {"start": v(-66.86, -69.98) * mm, "end": v(-63.63, -73.2) * mm});
            skLineSegment(sketch, "E14.5.0.2", {"start": v(-63.63, -73.2) * mm, "end": v(-60.4, -69.98) * mm});
            skLineSegment(sketch, "E14.5.0.3", {"start": v(-60.4, -69.98) * mm, "end": v(-63.63, -66.74) * mm});
            skLineSegment(sketch, "E14.5.1.0", {"start": v(-63.63, -57.85) * mm, "end": v(-66.86, -61.09) * mm});
            skLineSegment(sketch, "E14.5.1.1", {"start": v(-66.86, -61.09) * mm, "end": v(-63.63, -64.32) * mm});
            skLineSegment(sketch, "E14.5.1.2", {"start": v(-63.63, -64.32) * mm, "end": v(-60.4, -61.09) * mm});
            skLineSegment(sketch, "E14.5.1.3", {"start": v(-60.4, -61.09) * mm, "end": v(-63.63, -57.85) * mm});
            skLineSegment(sketch, "E14.5.2.0", {"start": v(-63.63, -48.96) * mm, "end": v(-66.86, -52.2) * mm});
            skLineSegment(sketch, "E14.5.2.1", {"start": v(-66.86, -52.2) * mm, "end": v(-63.63, -55.43) * mm});
            skLineSegment(sketch, "E14.5.2.2", {"start": v(-63.63, -55.43) * mm, "end": v(-60.4, -52.2) * mm});
            skLineSegment(sketch, "E14.5.2.3", {"start": v(-60.4, -52.2) * mm, "end": v(-63.63, -48.96) * mm});
            skLineSegment(sketch, "E14.5.3.0", {"start": v(-63.63, -40.07) * mm, "end": v(-66.86, -43.3) * mm});
            skLineSegment(sketch, "E14.5.3.1", {"start": v(-66.86, -43.3) * mm, "end": v(-63.63, -46.54) * mm});
            skLineSegment(sketch, "E14.5.3.2", {"start": v(-63.63, -46.54) * mm, "end": v(-60.4, -43.3) * mm});
            skLineSegment(sketch, "E14.5.3.3", {"start": v(-60.4, -43.3) * mm, "end": v(-63.63, -40.07) * mm});
            skLineSegment(sketch, "E14.5.4.0", {"start": v(-63.63, -31.18) * mm, "end": v(-66.86, -34.42) * mm});
            skLineSegment(sketch, "E14.5.4.1", {"start": v(-66.86, -34.42) * mm, "end": v(-63.63, -37.65) * mm});
            skLineSegment(sketch, "E14.5.4.2", {"start": v(-63.63, -37.65) * mm, "end": v(-60.4, -34.42) * mm});
            skLineSegment(sketch, "E14.5.4.3", {"start": v(-60.4, -34.42) * mm, "end": v(-63.63, -31.18) * mm});
            skLineSegment(sketch, "E14.5.5.0", {"start": v(-63.63, -22.3) * mm, "end": v(-66.86, -25.53) * mm});
            skLineSegment(sketch, "E14.5.5.1", {"start": v(-66.86, -25.53) * mm, "end": v(-63.63, -28.76) * mm});
            skLineSegment(sketch, "E14.5.5.2", {"start": v(-63.63, -28.76) * mm, "end": v(-60.4, -25.53) * mm});
            skLineSegment(sketch, "E14.5.5.3", {"start": v(-60.4, -25.53) * mm, "end": v(-63.63, -22.3) * mm});
            skLineSegment(sketch, "E14.5.6.0", {"start": v(-63.63, -13.4) * mm, "end": v(-66.86, -16.64) * mm});
            skLineSegment(sketch, "E14.5.6.1", {"start": v(-66.86, -16.64) * mm, "end": v(-63.63, -19.87) * mm});
            skLineSegment(sketch, "E14.5.6.2", {"start": v(-63.63, -19.87) * mm, "end": v(-60.4, -16.64) * mm});
            skLineSegment(sketch, "E14.5.6.3", {"start": v(-60.4, -16.64) * mm, "end": v(-63.63, -13.4) * mm});
            skLineSegment(sketch, "E14.5.7.0", {"start": v(-63.63, -4.51) * mm, "end": v(-66.86, -7.75) * mm});
            skLineSegment(sketch, "E14.5.7.1", {"start": v(-66.86, -7.75) * mm, "end": v(-63.63, -10.98) * mm});
            skLineSegment(sketch, "E14.5.7.2", {"start": v(-63.63, -10.98) * mm, "end": v(-60.4, -7.75) * mm});
            skLineSegment(sketch, "E14.5.7.3", {"start": v(-60.4, -7.75) * mm, "end": v(-63.63, -4.51) * mm});
            skLineSegment(sketch, "E14.6.0.0", {"start": v(-54.74, -66.74) * mm, "end": v(-57.97, -69.98) * mm});
            skLineSegment(sketch, "E14.6.0.1", {"start": v(-57.97, -69.98) * mm, "end": v(-54.74, -73.2) * mm});
            skLineSegment(sketch, "E14.6.0.2", {"start": v(-54.74, -73.2) * mm, "end": v(-51.5, -69.98) * mm});
            skLineSegment(sketch, "E14.6.0.3", {"start": v(-51.5, -69.98) * mm, "end": v(-54.74, -66.74) * mm});
            skLineSegment(sketch, "E14.6.1.0", {"start": v(-54.74, -57.85) * mm, "end": v(-57.97, -61.09) * mm});
            skLineSegment(sketch, "E14.6.1.1", {"start": v(-57.97, -61.09) * mm, "end": v(-54.74, -64.32) * mm});
            skLineSegment(sketch, "E14.6.1.2", {"start": v(-54.74, -64.32) * mm, "end": v(-51.5, -61.09) * mm});
            skLineSegment(sketch, "E14.6.1.3", {"start": v(-51.5, -61.09) * mm, "end": v(-54.74, -57.85) * mm});
            skLineSegment(sketch, "E14.6.2.0", {"start": v(-54.74, -48.96) * mm, "end": v(-57.97, -52.2) * mm});
            skLineSegment(sketch, "E14.6.2.1", {"start": v(-57.97, -52.2) * mm, "end": v(-54.74, -55.43) * mm});
            skLineSegment(sketch, "E14.6.2.2", {"start": v(-54.74, -55.43) * mm, "end": v(-51.5, -52.2) * mm});
            skLineSegment(sketch, "E14.6.2.3", {"start": v(-51.5, -52.2) * mm, "end": v(-54.74, -48.96) * mm});
            skLineSegment(sketch, "E14.6.3.0", {"start": v(-54.74, -40.07) * mm, "end": v(-57.97, -43.3) * mm});
            skLineSegment(sketch, "E14.6.3.1", {"start": v(-57.97, -43.3) * mm, "end": v(-54.74, -46.54) * mm});
            skLineSegment(sketch, "E14.6.3.2", {"start": v(-54.74, -46.54) * mm, "end": v(-51.5, -43.3) * mm});
            skLineSegment(sketch, "E14.6.3.3", {"start": v(-51.5, -43.3) * mm, "end": v(-54.74, -40.07) * mm});
            skLineSegment(sketch, "E14.6.4.0", {"start": v(-54.74, -31.18) * mm, "end": v(-57.97, -34.42) * mm});
            skLineSegment(sketch, "E14.6.4.1", {"start": v(-57.97, -34.42) * mm, "end": v(-54.74, -37.65) * mm});
            skLineSegment(sketch, "E14.6.4.2", {"start": v(-54.74, -37.65) * mm, "end": v(-51.5, -34.42) * mm});
            skLineSegment(sketch, "E14.6.4.3", {"start": v(-51.5, -34.42) * mm, "end": v(-54.74, -31.18) * mm});
            skLineSegment(sketch, "E14.6.5.0", {"start": v(-54.74, -22.3) * mm, "end": v(-57.97, -25.53) * mm});
            skLineSegment(sketch, "E14.6.5.1", {"start": v(-57.97, -25.53) * mm, "end": v(-54.74, -28.76) * mm});
            skLineSegment(sketch, "E14.6.5.2", {"start": v(-54.74, -28.76) * mm, "end": v(-51.5, -25.53) * mm});
            skLineSegment(sketch, "E14.6.5.3", {"start": v(-51.5, -25.53) * mm, "end": v(-54.74, -22.3) * mm});
            skLineSegment(sketch, "E14.6.6.0", {"start": v(-54.74, -13.4) * mm, "end": v(-57.97, -16.64) * mm});
            skLineSegment(sketch, "E14.6.6.1", {"start": v(-57.97, -16.64) * mm, "end": v(-54.74, -19.87) * mm});
            skLineSegment(sketch, "E14.6.6.2", {"start": v(-54.74, -19.87) * mm, "end": v(-51.5, -16.64) * mm});
            skLineSegment(sketch, "E14.6.6.3", {"start": v(-51.5, -16.64) * mm, "end": v(-54.74, -13.4) * mm});
            skLineSegment(sketch, "E14.6.7.0", {"start": v(-54.74, -4.51) * mm, "end": v(-57.97, -7.75) * mm});
            skLineSegment(sketch, "E14.6.7.1", {"start": v(-57.97, -7.75) * mm, "end": v(-54.74, -10.98) * mm});
            skLineSegment(sketch, "E14.6.7.2", {"start": v(-54.74, -10.98) * mm, "end": v(-51.5, -7.75) * mm});
            skLineSegment(sketch, "E14.6.7.3", {"start": v(-51.5, -7.75) * mm, "end": v(-54.74, -4.51) * mm});
            skLineSegment(sketch, "E14.7.0.0", {"start": v(-45.85, -66.74) * mm, "end": v(-49.08, -69.98) * mm});
            skLineSegment(sketch, "E14.7.0.1", {"start": v(-49.08, -69.98) * mm, "end": v(-45.85, -73.2) * mm});
            skLineSegment(sketch, "E14.7.0.2", {"start": v(-45.85, -73.2) * mm, "end": v(-42.61, -69.98) * mm});
            skLineSegment(sketch, "E14.7.0.3", {"start": v(-42.61, -69.98) * mm, "end": v(-45.85, -66.74) * mm});
            skLineSegment(sketch, "E14.7.1.0", {"start": v(-45.85, -57.85) * mm, "end": v(-49.08, -61.09) * mm});
            skLineSegment(sketch, "E14.7.1.1", {"start": v(-49.08, -61.09) * mm, "end": v(-45.85, -64.32) * mm});
            skLineSegment(sketch, "E14.7.1.2", {"start": v(-45.85, -64.32) * mm, "end": v(-42.61, -61.09) * mm});
            skLineSegment(sketch, "E14.7.1.3", {"start": v(-42.61, -61.09) * mm, "end": v(-45.85, -57.85) * mm});
            skLineSegment(sketch, "E14.7.2.0", {"start": v(-45.85, -48.96) * mm, "end": v(-49.08, -52.2) * mm});
            skLineSegment(sketch, "E14.7.2.1", {"start": v(-49.08, -52.2) * mm, "end": v(-45.85, -55.43) * mm});
            skLineSegment(sketch, "E14.7.2.2", {"start": v(-45.85, -55.43) * mm, "end": v(-42.61, -52.2) * mm});
            skLineSegment(sketch, "E14.7.2.3", {"start": v(-42.61, -52.2) * mm, "end": v(-45.85, -48.96) * mm});
            skLineSegment(sketch, "E14.7.3.0", {"start": v(-45.85, -40.07) * mm, "end": v(-49.08, -43.3) * mm});
            skLineSegment(sketch, "E14.7.3.1", {"start": v(-49.08, -43.3) * mm, "end": v(-45.85, -46.54) * mm});
            skLineSegment(sketch, "E14.7.3.2", {"start": v(-45.85, -46.54) * mm, "end": v(-42.61, -43.3) * mm});
            skLineSegment(sketch, "E14.7.3.3", {"start": v(-42.61, -43.3) * mm, "end": v(-45.85, -40.07) * mm});
            skLineSegment(sketch, "E14.7.4.0", {"start": v(-45.85, -31.18) * mm, "end": v(-49.08, -34.42) * mm});
            skLineSegment(sketch, "E14.7.4.1", {"start": v(-49.08, -34.42) * mm, "end": v(-45.85, -37.65) * mm});
            skLineSegment(sketch, "E14.7.4.2", {"start": v(-45.85, -37.65) * mm, "end": v(-42.61, -34.42) * mm});
            skLineSegment(sketch, "E14.7.4.3", {"start": v(-42.61, -34.42) * mm, "end": v(-45.85, -31.18) * mm});
            skLineSegment(sketch, "E14.7.5.0", {"start": v(-45.85, -22.3) * mm, "end": v(-49.08, -25.53) * mm});
            skLineSegment(sketch, "E14.7.5.1", {"start": v(-49.08, -25.53) * mm, "end": v(-45.85, -28.76) * mm});
            skLineSegment(sketch, "E14.7.5.2", {"start": v(-45.85, -28.76) * mm, "end": v(-42.61, -25.53) * mm});
            skLineSegment(sketch, "E14.7.5.3", {"start": v(-42.61, -25.53) * mm, "end": v(-45.85, -22.3) * mm});
            skLineSegment(sketch, "E14.7.6.0", {"start": v(-45.85, -13.4) * mm, "end": v(-49.08, -16.64) * mm});
            skLineSegment(sketch, "E14.7.6.1", {"start": v(-49.08, -16.64) * mm, "end": v(-45.85, -19.87) * mm});
            skLineSegment(sketch, "E14.7.6.2", {"start": v(-45.85, -19.87) * mm, "end": v(-42.61, -16.64) * mm});
            skLineSegment(sketch, "E14.7.6.3", {"start": v(-42.61, -16.64) * mm, "end": v(-45.85, -13.4) * mm});
            skLineSegment(sketch, "E14.7.7.0", {"start": v(-45.85, -4.51) * mm, "end": v(-49.08, -7.75) * mm});
            skLineSegment(sketch, "E14.7.7.1", {"start": v(-49.08, -7.75) * mm, "end": v(-45.85, -10.98) * mm});
            skLineSegment(sketch, "E14.7.7.2", {"start": v(-45.85, -10.98) * mm, "end": v(-42.61, -7.75) * mm});
            skLineSegment(sketch, "E14.7.7.3", {"start": v(-42.61, -7.75) * mm, "end": v(-45.85, -4.51) * mm});
            skLineSegment(sketch, "E14.8.0.0", {"start": v(-36.96, -66.74) * mm, "end": v(-40.19, -69.98) * mm});
            skLineSegment(sketch, "E14.8.0.1", {"start": v(-40.19, -69.98) * mm, "end": v(-36.96, -73.2) * mm});
            skLineSegment(sketch, "E14.8.0.2", {"start": v(-36.96, -73.2) * mm, "end": v(-33.72, -69.98) * mm});
            skLineSegment(sketch, "E14.8.0.3", {"start": v(-33.72, -69.98) * mm, "end": v(-36.96, -66.74) * mm});
            skLineSegment(sketch, "E14.8.1.0", {"start": v(-36.96, -57.85) * mm, "end": v(-40.19, -61.09) * mm});
            skLineSegment(sketch, "E14.8.1.1", {"start": v(-40.19, -61.09) * mm, "end": v(-36.96, -64.32) * mm});
            skLineSegment(sketch, "E14.8.1.2", {"start": v(-36.96, -64.32) * mm, "end": v(-33.72, -61.09) * mm});
            skLineSegment(sketch, "E14.8.1.3", {"start": v(-33.72, -61.09) * mm, "end": v(-36.96, -57.85) * mm});
            skLineSegment(sketch, "E14.8.2.0", {"start": v(-36.96, -48.96) * mm, "end": v(-40.19, -52.2) * mm});
            skLineSegment(sketch, "E14.8.2.1", {"start": v(-40.19, -52.2) * mm, "end": v(-36.96, -55.43) * mm});
            skLineSegment(sketch, "E14.8.2.2", {"start": v(-36.96, -55.43) * mm, "end": v(-33.72, -52.2) * mm});
            skLineSegment(sketch, "E14.8.2.3", {"start": v(-33.72, -52.2) * mm, "end": v(-36.96, -48.96) * mm});
            skLineSegment(sketch, "E14.8.3.0", {"start": v(-36.96, -40.07) * mm, "end": v(-40.19, -43.3) * mm});
            skLineSegment(sketch, "E14.8.3.1", {"start": v(-40.19, -43.3) * mm, "end": v(-36.96, -46.54) * mm});
            skLineSegment(sketch, "E14.8.3.2", {"start": v(-36.96, -46.54) * mm, "end": v(-33.72, -43.3) * mm});
            skLineSegment(sketch, "E14.8.3.3", {"start": v(-33.72, -43.3) * mm, "end": v(-36.96, -40.07) * mm});
            skLineSegment(sketch, "E14.8.4.0", {"start": v(-36.96, -31.18) * mm, "end": v(-40.19, -34.42) * mm});
            skLineSegment(sketch, "E14.8.4.1", {"start": v(-40.19, -34.42) * mm, "end": v(-36.96, -37.65) * mm});
            skLineSegment(sketch, "E14.8.4.2", {"start": v(-36.96, -37.65) * mm, "end": v(-33.72, -34.42) * mm});
            skLineSegment(sketch, "E14.8.4.3", {"start": v(-33.72, -34.42) * mm, "end": v(-36.96, -31.18) * mm});
            skLineSegment(sketch, "E14.8.5.0", {"start": v(-36.96, -22.3) * mm, "end": v(-40.19, -25.53) * mm});
            skLineSegment(sketch, "E14.8.5.1", {"start": v(-40.19, -25.53) * mm, "end": v(-36.96, -28.76) * mm});
            skLineSegment(sketch, "E14.8.5.2", {"start": v(-36.96, -28.76) * mm, "end": v(-33.72, -25.53) * mm});
            skLineSegment(sketch, "E14.8.5.3", {"start": v(-33.72, -25.53) * mm, "end": v(-36.96, -22.3) * mm});
            skLineSegment(sketch, "E14.8.6.0", {"start": v(-36.96, -13.4) * mm, "end": v(-40.19, -16.64) * mm});
            skLineSegment(sketch, "E14.8.6.1", {"start": v(-40.19, -16.64) * mm, "end": v(-36.96, -19.87) * mm});
            skLineSegment(sketch, "E14.8.6.2", {"start": v(-36.96, -19.87) * mm, "end": v(-33.72, -16.64) * mm});
            skLineSegment(sketch, "E14.8.6.3", {"start": v(-33.72, -16.64) * mm, "end": v(-36.96, -13.4) * mm});
            skLineSegment(sketch, "E14.8.7.0", {"start": v(-36.96, -4.51) * mm, "end": v(-40.19, -7.75) * mm});
            skLineSegment(sketch, "E14.8.7.1", {"start": v(-40.19, -7.75) * mm, "end": v(-36.96, -10.98) * mm});
            skLineSegment(sketch, "E14.8.7.2", {"start": v(-36.96, -10.98) * mm, "end": v(-33.72, -7.75) * mm});
            skLineSegment(sketch, "E14.8.7.3", {"start": v(-33.72, -7.75) * mm, "end": v(-36.96, -4.51) * mm});
            skLineSegment(sketch, "E14.9.0.0", {"start": v(-28.07, -66.74) * mm, "end": v(-31.3, -69.98) * mm});
            skLineSegment(sketch, "E14.9.0.1", {"start": v(-31.3, -69.98) * mm, "end": v(-28.07, -73.2) * mm});
            skLineSegment(sketch, "E14.9.0.2", {"start": v(-28.07, -73.2) * mm, "end": v(-24.83, -69.98) * mm});
            skLineSegment(sketch, "E14.9.0.3", {"start": v(-24.83, -69.98) * mm, "end": v(-28.07, -66.74) * mm});
            skLineSegment(sketch, "E14.9.1.0", {"start": v(-28.07, -57.85) * mm, "end": v(-31.3, -61.09) * mm});
            skLineSegment(sketch, "E14.9.1.1", {"start": v(-31.3, -61.09) * mm, "end": v(-28.07, -64.32) * mm});
            skLineSegment(sketch, "E14.9.1.2", {"start": v(-28.07, -64.32) * mm, "end": v(-24.83, -61.09) * mm});
            skLineSegment(sketch, "E14.9.1.3", {"start": v(-24.83, -61.09) * mm, "end": v(-28.07, -57.85) * mm});
            skLineSegment(sketch, "E14.9.2.0", {"start": v(-28.07, -48.96) * mm, "end": v(-31.3, -52.2) * mm});
            skLineSegment(sketch, "E14.9.2.1", {"start": v(-31.3, -52.2) * mm, "end": v(-28.07, -55.43) * mm});
            skLineSegment(sketch, "E14.9.2.2", {"start": v(-28.07, -55.43) * mm, "end": v(-24.83, -52.2) * mm});
            skLineSegment(sketch, "E14.9.2.3", {"start": v(-24.83, -52.2) * mm, "end": v(-28.07, -48.96) * mm});
            skLineSegment(sketch, "E14.9.3.0", {"start": v(-28.07, -40.07) * mm, "end": v(-31.3, -43.3) * mm});
            skLineSegment(sketch, "E14.9.3.1", {"start": v(-31.3, -43.3) * mm, "end": v(-28.07, -46.54) * mm});
            skLineSegment(sketch, "E14.9.3.2", {"start": v(-28.07, -46.54) * mm, "end": v(-24.83, -43.3) * mm});
            skLineSegment(sketch, "E14.9.3.3", {"start": v(-24.83, -43.3) * mm, "end": v(-28.07, -40.07) * mm});
            skLineSegment(sketch, "E14.9.4.0", {"start": v(-28.07, -31.18) * mm, "end": v(-31.3, -34.42) * mm});
            skLineSegment(sketch, "E14.9.4.1", {"start": v(-31.3, -34.42) * mm, "end": v(-28.07, -37.65) * mm});
            skLineSegment(sketch, "E14.9.4.2", {"start": v(-28.07, -37.65) * mm, "end": v(-24.83, -34.42) * mm});
            skLineSegment(sketch, "E14.9.4.3", {"start": v(-24.83, -34.42) * mm, "end": v(-28.07, -31.18) * mm});
            skLineSegment(sketch, "E14.9.5.0", {"start": v(-28.07, -22.3) * mm, "end": v(-31.3, -25.53) * mm});
            skLineSegment(sketch, "E14.9.5.1", {"start": v(-31.3, -25.53) * mm, "end": v(-28.07, -28.76) * mm});
            skLineSegment(sketch, "E14.9.5.2", {"start": v(-28.07, -28.76) * mm, "end": v(-24.83, -25.53) * mm});
            skLineSegment(sketch, "E14.9.5.3", {"start": v(-24.83, -25.53) * mm, "end": v(-28.07, -22.3) * mm});
            skLineSegment(sketch, "E14.9.6.0", {"start": v(-28.07, -13.4) * mm, "end": v(-31.3, -16.64) * mm});
            skLineSegment(sketch, "E14.9.6.1", {"start": v(-31.3, -16.64) * mm, "end": v(-28.07, -19.87) * mm});
            skLineSegment(sketch, "E14.9.6.2", {"start": v(-28.07, -19.87) * mm, "end": v(-24.83, -16.64) * mm});
            skLineSegment(sketch, "E14.9.6.3", {"start": v(-24.83, -16.64) * mm, "end": v(-28.07, -13.4) * mm});
            skLineSegment(sketch, "E14.9.7.0", {"start": v(-28.07, -4.51) * mm, "end": v(-31.3, -7.75) * mm});
            skLineSegment(sketch, "E14.9.7.1", {"start": v(-31.3, -7.75) * mm, "end": v(-28.07, -10.98) * mm});
            skLineSegment(sketch, "E14.9.7.2", {"start": v(-28.07, -10.98) * mm, "end": v(-24.83, -7.75) * mm});
            skLineSegment(sketch, "E14.9.7.3", {"start": v(-24.83, -7.75) * mm, "end": v(-28.07, -4.51) * mm});
            skLineSegment(sketch, "E14.10.0.0", {"start": v(-19.18, -66.74) * mm, "end": v(-22.4, -69.98) * mm});
            skLineSegment(sketch, "E14.10.0.1", {"start": v(-22.4, -69.98) * mm, "end": v(-19.18, -73.2) * mm});
            skLineSegment(sketch, "E14.10.0.2", {"start": v(-19.18, -73.2) * mm, "end": v(-15.94, -69.98) * mm});
            skLineSegment(sketch, "E14.10.0.3", {"start": v(-15.94, -69.98) * mm, "end": v(-19.18, -66.74) * mm});
            skLineSegment(sketch, "E14.10.1.0", {"start": v(-19.18, -57.85) * mm, "end": v(-22.4, -61.09) * mm});
            skLineSegment(sketch, "E14.10.1.1", {"start": v(-22.4, -61.09) * mm, "end": v(-19.18, -64.32) * mm});
            skLineSegment(sketch, "E14.10.1.2", {"start": v(-19.18, -64.32) * mm, "end": v(-15.94, -61.09) * mm});
            skLineSegment(sketch, "E14.10.1.3", {"start": v(-15.94, -61.09) * mm, "end": v(-19.18, -57.85) * mm});
            skLineSegment(sketch, "E14.10.2.0", {"start": v(-19.18, -48.96) * mm, "end": v(-22.4, -52.2) * mm});
            skLineSegment(sketch, "E14.10.2.1", {"start": v(-22.4, -52.2) * mm, "end": v(-19.18, -55.43) * mm});
            skLineSegment(sketch, "E14.10.2.2", {"start": v(-19.18, -55.43) * mm, "end": v(-15.94, -52.2) * mm});
            skLineSegment(sketch, "E14.10.2.3", {"start": v(-15.94, -52.2) * mm, "end": v(-19.18, -48.96) * mm});
            skLineSegment(sketch, "E14.10.3.0", {"start": v(-19.18, -40.07) * mm, "end": v(-22.4, -43.3) * mm});
            skLineSegment(sketch, "E14.10.3.1", {"start": v(-22.4, -43.3) * mm, "end": v(-19.18, -46.54) * mm});
            skLineSegment(sketch, "E14.10.3.2", {"start": v(-19.18, -46.54) * mm, "end": v(-15.94, -43.3) * mm});
            skLineSegment(sketch, "E14.10.3.3", {"start": v(-15.94, -43.3) * mm, "end": v(-19.18, -40.07) * mm});
            skLineSegment(sketch, "E14.10.4.0", {"start": v(-19.18, -31.18) * mm, "end": v(-22.4, -34.42) * mm});
            skLineSegment(sketch, "E14.10.4.1", {"start": v(-22.4, -34.42) * mm, "end": v(-19.18, -37.65) * mm});
            skLineSegment(sketch, "E14.10.4.2", {"start": v(-19.18, -37.65) * mm, "end": v(-15.94, -34.42) * mm});
            skLineSegment(sketch, "E14.10.4.3", {"start": v(-15.94, -34.42) * mm, "end": v(-19.18, -31.18) * mm});
            skLineSegment(sketch, "E14.10.5.0", {"start": v(-19.18, -22.3) * mm, "end": v(-22.4, -25.53) * mm});
            skLineSegment(sketch, "E14.10.5.1", {"start": v(-22.4, -25.53) * mm, "end": v(-19.18, -28.76) * mm});
            skLineSegment(sketch, "E14.10.5.2", {"start": v(-19.18, -28.76) * mm, "end": v(-15.94, -25.53) * mm});
            skLineSegment(sketch, "E14.10.5.3", {"start": v(-15.94, -25.53) * mm, "end": v(-19.18, -22.3) * mm});
            skLineSegment(sketch, "E14.10.6.0", {"start": v(-19.18, -13.4) * mm, "end": v(-22.4, -16.64) * mm});
            skLineSegment(sketch, "E14.10.6.1", {"start": v(-22.4, -16.64) * mm, "end": v(-19.18, -19.87) * mm});
            skLineSegment(sketch, "E14.10.6.2", {"start": v(-19.18, -19.87) * mm, "end": v(-15.94, -16.64) * mm});
            skLineSegment(sketch, "E14.10.6.3", {"start": v(-15.94, -16.64) * mm, "end": v(-19.18, -13.4) * mm});
            skLineSegment(sketch, "E14.10.7.0", {"start": v(-19.18, -4.51) * mm, "end": v(-22.4, -7.75) * mm});
            skLineSegment(sketch, "E14.10.7.1", {"start": v(-22.4, -7.75) * mm, "end": v(-19.18, -10.98) * mm});
            skLineSegment(sketch, "E14.10.7.2", {"start": v(-19.18, -10.98) * mm, "end": v(-15.94, -7.75) * mm});
            skLineSegment(sketch, "E14.10.7.3", {"start": v(-15.94, -7.75) * mm, "end": v(-19.18, -4.51) * mm});
            skLineSegment(sketch, "E14.11.0.0", {"start": v(-10.29, -66.74) * mm, "end": v(-13.52, -69.98) * mm});
            skLineSegment(sketch, "E14.11.0.1", {"start": v(-13.52, -69.98) * mm, "end": v(-10.29, -73.2) * mm});
            skLineSegment(sketch, "E14.11.0.2", {"start": v(-10.29, -73.2) * mm, "end": v(-7.05, -69.98) * mm});
            skLineSegment(sketch, "E14.11.0.3", {"start": v(-7.05, -69.98) * mm, "end": v(-10.29, -66.74) * mm});
            skLineSegment(sketch, "E14.11.1.0", {"start": v(-10.29, -57.85) * mm, "end": v(-13.52, -61.09) * mm});
            skLineSegment(sketch, "E14.11.1.1", {"start": v(-13.52, -61.09) * mm, "end": v(-10.29, -64.32) * mm});
            skLineSegment(sketch, "E14.11.1.2", {"start": v(-10.29, -64.32) * mm, "end": v(-7.05, -61.09) * mm});
            skLineSegment(sketch, "E14.11.1.3", {"start": v(-7.05, -61.09) * mm, "end": v(-10.29, -57.85) * mm});
            skLineSegment(sketch, "E14.11.2.0", {"start": v(-10.29, -48.96) * mm, "end": v(-13.52, -52.2) * mm});
            skLineSegment(sketch, "E14.11.2.1", {"start": v(-13.52, -52.2) * mm, "end": v(-10.29, -55.43) * mm});
            skLineSegment(sketch, "E14.11.2.2", {"start": v(-10.29, -55.43) * mm, "end": v(-7.05, -52.2) * mm});
            skLineSegment(sketch, "E14.11.2.3", {"start": v(-7.05, -52.2) * mm, "end": v(-10.29, -48.96) * mm});
            skLineSegment(sketch, "E14.11.3.0", {"start": v(-10.29, -40.07) * mm, "end": v(-13.52, -43.3) * mm});
            skLineSegment(sketch, "E14.11.3.1", {"start": v(-13.52, -43.3) * mm, "end": v(-10.29, -46.54) * mm});
            skLineSegment(sketch, "E14.11.3.2", {"start": v(-10.29, -46.54) * mm, "end": v(-7.05, -43.3) * mm});
            skLineSegment(sketch, "E14.11.3.3", {"start": v(-7.05, -43.3) * mm, "end": v(-10.29, -40.07) * mm});
            skLineSegment(sketch, "E14.11.4.0", {"start": v(-10.29, -31.18) * mm, "end": v(-13.52, -34.42) * mm});
            skLineSegment(sketch, "E14.11.4.1", {"start": v(-13.52, -34.42) * mm, "end": v(-10.29, -37.65) * mm});
            skLineSegment(sketch, "E14.11.4.2", {"start": v(-10.29, -37.65) * mm, "end": v(-7.05, -34.42) * mm});
            skLineSegment(sketch, "E14.11.4.3", {"start": v(-7.05, -34.42) * mm, "end": v(-10.29, -31.18) * mm});
            skLineSegment(sketch, "E14.11.5.0", {"start": v(-10.29, -22.3) * mm, "end": v(-13.52, -25.53) * mm});
            skLineSegment(sketch, "E14.11.5.1", {"start": v(-13.52, -25.53) * mm, "end": v(-10.29, -28.76) * mm});
            skLineSegment(sketch, "E14.11.5.2", {"start": v(-10.29, -28.76) * mm, "end": v(-7.05, -25.53) * mm});
            skLineSegment(sketch, "E14.11.5.3", {"start": v(-7.05, -25.53) * mm, "end": v(-10.29, -22.3) * mm});
            skLineSegment(sketch, "E14.11.6.0", {"start": v(-10.29, -13.4) * mm, "end": v(-13.52, -16.64) * mm});
            skLineSegment(sketch, "E14.11.6.1", {"start": v(-13.52, -16.64) * mm, "end": v(-10.29, -19.87) * mm});
            skLineSegment(sketch, "E14.11.6.2", {"start": v(-10.29, -19.87) * mm, "end": v(-7.05, -16.64) * mm});
            skLineSegment(sketch, "E14.11.6.3", {"start": v(-7.05, -16.64) * mm, "end": v(-10.29, -13.4) * mm});
            skLineSegment(sketch, "E14.11.7.0", {"start": v(-10.29, -4.51) * mm, "end": v(-13.52, -7.75) * mm});
            skLineSegment(sketch, "E14.11.7.1", {"start": v(-13.52, -7.75) * mm, "end": v(-10.29, -10.98) * mm});
            skLineSegment(sketch, "E14.11.7.2", {"start": v(-10.29, -10.98) * mm, "end": v(-7.05, -7.75) * mm});
            skLineSegment(sketch, "E14.11.7.3", {"start": v(-7.05, -7.75) * mm, "end": v(-10.29, -4.51) * mm});
            skLineSegment(sketch, "E14.direction1", {"start": v(-108.08, -73.2) * mm, "end": v(-99.19, -73.2) * mm, "construction": true});
            skLineSegment(sketch, "E14.direction2", {"start": v(-108.08, -73.2) * mm, "end": v(-108.08, -64.32) * mm, "construction": true});
            skSolve(sketch);
        }
        {
            var Q0;
            Q0=qCreatedBy(makeId("Top.planeOp"),FACE);
            cPlane(context, id + "F3", {"entities" : qUnion([Q0]), "cplaneType" : CPlaneType.OFFSET, "offset" : 5 * mm, "width" : 152.4 * mm, "height" : 152.4 * mm});
        }
        {
            var Q0;
            Q0=qCreatedBy(id+"F3.planeOp",FACE);
            var sketch = newSketch(context, id + "F4", { "sketchPlane" : qUnion([Q0])});
            skLineSegment(sketch, "E15", {"start": v(-108.08, 71.41) * mm, "end": v(-106.64, 69.98) * mm});
            skLineSegment(sketch, "E16", {"start": v(-106.64, 69.98) * mm, "end": v(-108.08, 68.54) * mm});
            skLineSegment(sketch, "E17", {"start": v(-108.08, 68.54) * mm, "end": v(-109.51, 69.98) * mm});
            skLineSegment(sketch, "E18", {"start": v(-109.51, 69.98) * mm, "end": v(-108.08, 71.41) * mm});
            skLineSegment(sketch, "E19", {"start": v(-103.63, 74.42) * mm, "end": v(-112.52, 74.42) * mm, "construction": true});
            skLineSegment(sketch, "E20", {"start": v(-112.52, 74.42) * mm, "end": v(-112.52, 65.53) * mm, "construction": true});
            skLineSegment(sketch, "E21.0.1.0", {"start": v(-109.51, 61.09) * mm, "end": v(-108.08, 62.52) * mm});
            skLineSegment(sketch, "E21.0.1.1", {"start": v(-108.08, 59.65) * mm, "end": v(-109.51, 61.09) * mm});
            skLineSegment(sketch, "E21.0.1.2", {"start": v(-106.64, 61.09) * mm, "end": v(-108.08, 59.65) * mm});
            skLineSegment(sketch, "E21.0.1.3", {"start": v(-108.08, 62.52) * mm, "end": v(-106.64, 61.09) * mm});
            skLineSegment(sketch, "E21.0.2.0", {"start": v(-109.51, 52.2) * mm, "end": v(-108.08, 53.63) * mm});
            skLineSegment(sketch, "E21.0.2.1", {"start": v(-108.08, 50.76) * mm, "end": v(-109.51, 52.2) * mm});
            skLineSegment(sketch, "E21.0.2.2", {"start": v(-106.64, 52.2) * mm, "end": v(-108.08, 50.76) * mm});
            skLineSegment(sketch, "E21.0.2.3", {"start": v(-108.08, 53.63) * mm, "end": v(-106.64, 52.2) * mm});
            skLineSegment(sketch, "E21.0.3.0", {"start": v(-109.51, 43.3) * mm, "end": v(-108.08, 44.74) * mm});
            skLineSegment(sketch, "E21.0.3.1", {"start": v(-108.08, 41.87) * mm, "end": v(-109.51, 43.3) * mm});
            skLineSegment(sketch, "E21.0.3.2", {"start": v(-106.64, 43.3) * mm, "end": v(-108.08, 41.87) * mm});
            skLineSegment(sketch, "E21.0.3.3", {"start": v(-108.08, 44.74) * mm, "end": v(-106.64, 43.3) * mm});
            skLineSegment(sketch, "E21.0.4.0", {"start": v(-109.51, 34.42) * mm, "end": v(-108.08, 35.85) * mm});
            skLineSegment(sketch, "E21.0.4.1", {"start": v(-108.08, 32.98) * mm, "end": v(-109.51, 34.42) * mm});
            skLineSegment(sketch, "E21.0.4.2", {"start": v(-106.64, 34.42) * mm, "end": v(-108.08, 32.98) * mm});
            skLineSegment(sketch, "E21.0.4.3", {"start": v(-108.08, 35.85) * mm, "end": v(-106.64, 34.42) * mm});
            skLineSegment(sketch, "E21.0.5.0", {"start": v(-109.51, 25.53) * mm, "end": v(-108.08, 26.96) * mm});
            skLineSegment(sketch, "E21.0.5.1", {"start": v(-108.08, 24.1) * mm, "end": v(-109.51, 25.53) * mm});
            skLineSegment(sketch, "E21.0.5.2", {"start": v(-106.64, 25.53) * mm, "end": v(-108.08, 24.1) * mm});
            skLineSegment(sketch, "E21.0.5.3", {"start": v(-108.08, 26.96) * mm, "end": v(-106.64, 25.53) * mm});
            skLineSegment(sketch, "E21.0.6.0", {"start": v(-109.51, 16.64) * mm, "end": v(-108.08, 18.07) * mm});
            skLineSegment(sketch, "E21.0.6.1", {"start": v(-108.08, 15.2) * mm, "end": v(-109.51, 16.64) * mm});
            skLineSegment(sketch, "E21.0.6.2", {"start": v(-106.64, 16.64) * mm, "end": v(-108.08, 15.2) * mm});
            skLineSegment(sketch, "E21.0.6.3", {"start": v(-108.08, 18.07) * mm, "end": v(-106.64, 16.64) * mm});
            skLineSegment(sketch, "E21.0.7.0", {"start": v(-109.51, 7.75) * mm, "end": v(-108.08, 9.18) * mm});
            skLineSegment(sketch, "E21.0.7.1", {"start": v(-108.08, 6.31) * mm, "end": v(-109.51, 7.75) * mm});
            skLineSegment(sketch, "E21.0.7.2", {"start": v(-106.64, 7.75) * mm, "end": v(-108.08, 6.31) * mm});
            skLineSegment(sketch, "E21.0.7.3", {"start": v(-108.08, 9.18) * mm, "end": v(-106.64, 7.75) * mm});
            skLineSegment(sketch, "E21.1.0.0", {"start": v(-100.62, 69.98) * mm, "end": v(-99.19, 71.41) * mm});
            skLineSegment(sketch, "E21.1.0.1", {"start": v(-99.19, 68.54) * mm, "end": v(-100.62, 69.98) * mm});
            skLineSegment(sketch, "E21.1.0.2", {"start": v(-97.75, 69.98) * mm, "end": v(-99.19, 68.54) * mm});
            skLineSegment(sketch, "E21.1.0.3", {"start": v(-99.19, 71.41) * mm, "end": v(-97.75, 69.98) * mm});
            skLineSegment(sketch, "E21.1.1.0", {"start": v(-100.62, 61.09) * mm, "end": v(-99.19, 62.52) * mm});
            skLineSegment(sketch, "E21.1.1.1", {"start": v(-99.19, 59.65) * mm, "end": v(-100.62, 61.09) * mm});
            skLineSegment(sketch, "E21.1.1.2", {"start": v(-97.75, 61.09) * mm, "end": v(-99.19, 59.65) * mm});
            skLineSegment(sketch, "E21.1.1.3", {"start": v(-99.19, 62.52) * mm, "end": v(-97.75, 61.09) * mm});
            skLineSegment(sketch, "E21.1.2.0", {"start": v(-100.62, 52.2) * mm, "end": v(-99.19, 53.63) * mm});
            skLineSegment(sketch, "E21.1.2.1", {"start": v(-99.19, 50.76) * mm, "end": v(-100.62, 52.2) * mm});
            skLineSegment(sketch, "E21.1.2.2", {"start": v(-97.75, 52.2) * mm, "end": v(-99.19, 50.76) * mm});
            skLineSegment(sketch, "E21.1.2.3", {"start": v(-99.19, 53.63) * mm, "end": v(-97.75, 52.2) * mm});
            skLineSegment(sketch, "E21.1.3.0", {"start": v(-100.62, 43.3) * mm, "end": v(-99.19, 44.74) * mm});
            skLineSegment(sketch, "E21.1.3.1", {"start": v(-99.19, 41.87) * mm, "end": v(-100.62, 43.3) * mm});
            skLineSegment(sketch, "E21.1.3.2", {"start": v(-97.75, 43.3) * mm, "end": v(-99.19, 41.87) * mm});
            skLineSegment(sketch, "E21.1.3.3", {"start": v(-99.19, 44.74) * mm, "end": v(-97.75, 43.3) * mm});
            skLineSegment(sketch, "E21.1.4.0", {"start": v(-100.62, 34.42) * mm, "end": v(-99.19, 35.85) * mm});
            skLineSegment(sketch, "E21.1.4.1", {"start": v(-99.19, 32.98) * mm, "end": v(-100.62, 34.42) * mm});
            skLineSegment(sketch, "E21.1.4.2", {"start": v(-97.75, 34.42) * mm, "end": v(-99.19, 32.98) * mm});
            skLineSegment(sketch, "E21.1.4.3", {"start": v(-99.19, 35.85) * mm, "end": v(-97.75, 34.42) * mm});
            skLineSegment(sketch, "E21.1.5.0", {"start": v(-100.62, 25.53) * mm, "end": v(-99.19, 26.96) * mm});
            skLineSegment(sketch, "E21.1.5.1", {"start": v(-99.19, 24.1) * mm, "end": v(-100.62, 25.53) * mm});
            skLineSegment(sketch, "E21.1.5.2", {"start": v(-97.75, 25.53) * mm, "end": v(-99.19, 24.1) * mm});
            skLineSegment(sketch, "E21.1.5.3", {"start": v(-99.19, 26.96) * mm, "end": v(-97.75, 25.53) * mm});
            skLineSegment(sketch, "E21.1.6.0", {"start": v(-100.62, 16.64) * mm, "end": v(-99.19, 18.07) * mm});
            skLineSegment(sketch, "E21.1.6.1", {"start": v(-99.19, 15.2) * mm, "end": v(-100.62, 16.64) * mm});
            skLineSegment(sketch, "E21.1.6.2", {"start": v(-97.75, 16.64) * mm, "end": v(-99.19, 15.2) * mm});
            skLineSegment(sketch, "E21.1.6.3", {"start": v(-99.19, 18.07) * mm, "end": v(-97.75, 16.64) * mm});
            skLineSegment(sketch, "E21.1.7.0", {"start": v(-100.62, 7.75) * mm, "end": v(-99.19, 9.18) * mm});
            skLineSegment(sketch, "E21.1.7.1", {"start": v(-99.19, 6.31) * mm, "end": v(-100.62, 7.75) * mm});
            skLineSegment(sketch, "E21.1.7.2", {"start": v(-97.75, 7.75) * mm, "end": v(-99.19, 6.31) * mm});
            skLineSegment(sketch, "E21.1.7.3", {"start": v(-99.19, 9.18) * mm, "end": v(-97.75, 7.75) * mm});
            skLineSegment(sketch, "E21.2.0.0", {"start": v(-91.73, 69.98) * mm, "end": v(-90.3, 71.41) * mm});
            skLineSegment(sketch, "E21.2.0.1", {"start": v(-90.3, 68.54) * mm, "end": v(-91.73, 69.98) * mm});
            skLineSegment(sketch, "E21.2.0.2", {"start": v(-88.86, 69.98) * mm, "end": v(-90.3, 68.54) * mm});
            skLineSegment(sketch, "E21.2.0.3", {"start": v(-90.3, 71.41) * mm, "end": v(-88.86, 69.98) * mm});
            skLineSegment(sketch, "E21.2.1.0", {"start": v(-91.73, 61.09) * mm, "end": v(-90.3, 62.52) * mm});
            skLineSegment(sketch, "E21.2.1.1", {"start": v(-90.3, 59.65) * mm, "end": v(-91.73, 61.09) * mm});
            skLineSegment(sketch, "E21.2.1.2", {"start": v(-88.86, 61.09) * mm, "end": v(-90.3, 59.65) * mm});
            skLineSegment(sketch, "E21.2.1.3", {"start": v(-90.3, 62.52) * mm, "end": v(-88.86, 61.09) * mm});
            skLineSegment(sketch, "E21.2.2.0", {"start": v(-91.73, 52.2) * mm, "end": v(-90.3, 53.63) * mm});
            skLineSegment(sketch, "E21.2.2.1", {"start": v(-90.3, 50.76) * mm, "end": v(-91.73, 52.2) * mm});
            skLineSegment(sketch, "E21.2.2.2", {"start": v(-88.86, 52.2) * mm, "end": v(-90.3, 50.76) * mm});
            skLineSegment(sketch, "E21.2.2.3", {"start": v(-90.3, 53.63) * mm, "end": v(-88.86, 52.2) * mm});
            skLineSegment(sketch, "E21.2.3.0", {"start": v(-91.73, 43.3) * mm, "end": v(-90.3, 44.74) * mm});
            skLineSegment(sketch, "E21.2.3.1", {"start": v(-90.3, 41.87) * mm, "end": v(-91.73, 43.3) * mm});
            skLineSegment(sketch, "E21.2.3.2", {"start": v(-88.86, 43.3) * mm, "end": v(-90.3, 41.87) * mm});
            skLineSegment(sketch, "E21.2.3.3", {"start": v(-90.3, 44.74) * mm, "end": v(-88.86, 43.3) * mm});
            skLineSegment(sketch, "E21.2.4.0", {"start": v(-91.73, 34.42) * mm, "end": v(-90.3, 35.85) * mm});
            skLineSegment(sketch, "E21.2.4.1", {"start": v(-90.3, 32.98) * mm, "end": v(-91.73, 34.42) * mm});
            skLineSegment(sketch, "E21.2.4.2", {"start": v(-88.86, 34.42) * mm, "end": v(-90.3, 32.98) * mm});
            skLineSegment(sketch, "E21.2.4.3", {"start": v(-90.3, 35.85) * mm, "end": v(-88.86, 34.42) * mm});
            skLineSegment(sketch, "E21.2.5.0", {"start": v(-91.73, 25.53) * mm, "end": v(-90.3, 26.96) * mm});
            skLineSegment(sketch, "E21.2.5.1", {"start": v(-90.3, 24.1) * mm, "end": v(-91.73, 25.53) * mm});
            skLineSegment(sketch, "E21.2.5.2", {"start": v(-88.86, 25.53) * mm, "end": v(-90.3, 24.1) * mm});
            skLineSegment(sketch, "E21.2.5.3", {"start": v(-90.3, 26.96) * mm, "end": v(-88.86, 25.53) * mm});
            skLineSegment(sketch, "E21.2.6.0", {"start": v(-91.73, 16.64) * mm, "end": v(-90.3, 18.07) * mm});
            skLineSegment(sketch, "E21.2.6.1", {"start": v(-90.3, 15.2) * mm, "end": v(-91.73, 16.64) * mm});
            skLineSegment(sketch, "E21.2.6.2", {"start": v(-88.86, 16.64) * mm, "end": v(-90.3, 15.2) * mm});
            skLineSegment(sketch, "E21.2.6.3", {"start": v(-90.3, 18.07) * mm, "end": v(-88.86, 16.64) * mm});
            skLineSegment(sketch, "E21.2.7.0", {"start": v(-91.73, 7.75) * mm, "end": v(-90.3, 9.18) * mm});
            skLineSegment(sketch, "E21.2.7.1", {"start": v(-90.3, 6.31) * mm, "end": v(-91.73, 7.75) * mm});
            skLineSegment(sketch, "E21.2.7.2", {"start": v(-88.86, 7.75) * mm, "end": v(-90.3, 6.31) * mm});
            skLineSegment(sketch, "E21.2.7.3", {"start": v(-90.3, 9.18) * mm, "end": v(-88.86, 7.75) * mm});
            skLineSegment(sketch, "E21.3.0.0", {"start": v(-82.84, 69.98) * mm, "end": v(-81.4, 71.41) * mm});
            skLineSegment(sketch, "E21.3.0.1", {"start": v(-81.4, 68.54) * mm, "end": v(-82.84, 69.98) * mm});
            skLineSegment(sketch, "E21.3.0.2", {"start": v(-79.97, 69.98) * mm, "end": v(-81.4, 68.54) * mm});
            skLineSegment(sketch, "E21.3.0.3", {"start": v(-81.4, 71.41) * mm, "end": v(-79.97, 69.98) * mm});
            skLineSegment(sketch, "E21.3.1.0", {"start": v(-82.84, 61.09) * mm, "end": v(-81.4, 62.52) * mm});
            skLineSegment(sketch, "E21.3.1.1", {"start": v(-81.4, 59.65) * mm, "end": v(-82.84, 61.09) * mm});
            skLineSegment(sketch, "E21.3.1.2", {"start": v(-79.97, 61.09) * mm, "end": v(-81.4, 59.65) * mm});
            skLineSegment(sketch, "E21.3.1.3", {"start": v(-81.4, 62.52) * mm, "end": v(-79.97, 61.09) * mm});
            skLineSegment(sketch, "E21.3.2.0", {"start": v(-82.84, 52.2) * mm, "end": v(-81.4, 53.63) * mm});
            skLineSegment(sketch, "E21.3.2.1", {"start": v(-81.4, 50.76) * mm, "end": v(-82.84, 52.2) * mm});
            skLineSegment(sketch, "E21.3.2.2", {"start": v(-79.97, 52.2) * mm, "end": v(-81.4, 50.76) * mm});
            skLineSegment(sketch, "E21.3.2.3", {"start": v(-81.4, 53.63) * mm, "end": v(-79.97, 52.2) * mm});
            skLineSegment(sketch, "E21.3.3.0", {"start": v(-82.84, 43.3) * mm, "end": v(-81.4, 44.74) * mm});
            skLineSegment(sketch, "E21.3.3.1", {"start": v(-81.4, 41.87) * mm, "end": v(-82.84, 43.3) * mm});
            skLineSegment(sketch, "E21.3.3.2", {"start": v(-79.97, 43.3) * mm, "end": v(-81.4, 41.87) * mm});
            skLineSegment(sketch, "E21.3.3.3", {"start": v(-81.4, 44.74) * mm, "end": v(-79.97, 43.3) * mm});
            skLineSegment(sketch, "E21.3.4.0", {"start": v(-82.84, 34.42) * mm, "end": v(-81.4, 35.85) * mm});
            skLineSegment(sketch, "E21.3.4.1", {"start": v(-81.4, 32.98) * mm, "end": v(-82.84, 34.42) * mm});
            skLineSegment(sketch, "E21.3.4.2", {"start": v(-79.97, 34.42) * mm, "end": v(-81.4, 32.98) * mm});
            skLineSegment(sketch, "E21.3.4.3", {"start": v(-81.4, 35.85) * mm, "end": v(-79.97, 34.42) * mm});
            skLineSegment(sketch, "E21.3.5.0", {"start": v(-82.84, 25.53) * mm, "end": v(-81.4, 26.96) * mm});
            skLineSegment(sketch, "E21.3.5.1", {"start": v(-81.4, 24.1) * mm, "end": v(-82.84, 25.53) * mm});
            skLineSegment(sketch, "E21.3.5.2", {"start": v(-79.97, 25.53) * mm, "end": v(-81.4, 24.1) * mm});
            skLineSegment(sketch, "E21.3.5.3", {"start": v(-81.4, 26.96) * mm, "end": v(-79.97, 25.53) * mm});
            skLineSegment(sketch, "E21.3.6.0", {"start": v(-82.84, 16.64) * mm, "end": v(-81.4, 18.07) * mm});
            skLineSegment(sketch, "E21.3.6.1", {"start": v(-81.4, 15.2) * mm, "end": v(-82.84, 16.64) * mm});
            skLineSegment(sketch, "E21.3.6.2", {"start": v(-79.97, 16.64) * mm, "end": v(-81.4, 15.2) * mm});
            skLineSegment(sketch, "E21.3.6.3", {"start": v(-81.4, 18.07) * mm, "end": v(-79.97, 16.64) * mm});
            skLineSegment(sketch, "E21.3.7.0", {"start": v(-82.84, 7.75) * mm, "end": v(-81.4, 9.18) * mm});
            skLineSegment(sketch, "E21.3.7.1", {"start": v(-81.4, 6.31) * mm, "end": v(-82.84, 7.75) * mm});
            skLineSegment(sketch, "E21.3.7.2", {"start": v(-79.97, 7.75) * mm, "end": v(-81.4, 6.31) * mm});
            skLineSegment(sketch, "E21.3.7.3", {"start": v(-81.4, 9.18) * mm, "end": v(-79.97, 7.75) * mm});
            skLineSegment(sketch, "E21.4.0.0", {"start": v(-73.95, 69.98) * mm, "end": v(-72.52, 71.41) * mm});
            skLineSegment(sketch, "E21.4.0.1", {"start": v(-72.52, 68.54) * mm, "end": v(-73.95, 69.98) * mm});
            skLineSegment(sketch, "E21.4.0.2", {"start": v(-71.08, 69.98) * mm, "end": v(-72.52, 68.54) * mm});
            skLineSegment(sketch, "E21.4.0.3", {"start": v(-72.52, 71.41) * mm, "end": v(-71.08, 69.98) * mm});
            skLineSegment(sketch, "E21.4.1.0", {"start": v(-73.95, 61.09) * mm, "end": v(-72.52, 62.52) * mm});
            skLineSegment(sketch, "E21.4.1.1", {"start": v(-72.52, 59.65) * mm, "end": v(-73.95, 61.09) * mm});
            skLineSegment(sketch, "E21.4.1.2", {"start": v(-71.08, 61.09) * mm, "end": v(-72.52, 59.65) * mm});
            skLineSegment(sketch, "E21.4.1.3", {"start": v(-72.52, 62.52) * mm, "end": v(-71.08, 61.09) * mm});
            skLineSegment(sketch, "E21.4.2.0", {"start": v(-73.95, 52.2) * mm, "end": v(-72.52, 53.63) * mm});
            skLineSegment(sketch, "E21.4.2.1", {"start": v(-72.52, 50.76) * mm, "end": v(-73.95, 52.2) * mm});
            skLineSegment(sketch, "E21.4.2.2", {"start": v(-71.08, 52.2) * mm, "end": v(-72.52, 50.76) * mm});
            skLineSegment(sketch, "E21.4.2.3", {"start": v(-72.52, 53.63) * mm, "end": v(-71.08, 52.2) * mm});
            skLineSegment(sketch, "E21.4.3.0", {"start": v(-73.95, 43.3) * mm, "end": v(-72.52, 44.74) * mm});
            skLineSegment(sketch, "E21.4.3.1", {"start": v(-72.52, 41.87) * mm, "end": v(-73.95, 43.3) * mm});
            skLineSegment(sketch, "E21.4.3.2", {"start": v(-71.08, 43.3) * mm, "end": v(-72.52, 41.87) * mm});
            skLineSegment(sketch, "E21.4.3.3", {"start": v(-72.52, 44.74) * mm, "end": v(-71.08, 43.3) * mm});
            skLineSegment(sketch, "E21.4.4.0", {"start": v(-73.95, 34.42) * mm, "end": v(-72.52, 35.85) * mm});
            skLineSegment(sketch, "E21.4.4.1", {"start": v(-72.52, 32.98) * mm, "end": v(-73.95, 34.42) * mm});
            skLineSegment(sketch, "E21.4.4.2", {"start": v(-71.08, 34.42) * mm, "end": v(-72.52, 32.98) * mm});
            skLineSegment(sketch, "E21.4.4.3", {"start": v(-72.52, 35.85) * mm, "end": v(-71.08, 34.42) * mm});
            skLineSegment(sketch, "E21.4.5.0", {"start": v(-73.95, 25.53) * mm, "end": v(-72.52, 26.96) * mm});
            skLineSegment(sketch, "E21.4.5.1", {"start": v(-72.52, 24.1) * mm, "end": v(-73.95, 25.53) * mm});
            skLineSegment(sketch, "E21.4.5.2", {"start": v(-71.08, 25.53) * mm, "end": v(-72.52, 24.1) * mm});
            skLineSegment(sketch, "E21.4.5.3", {"start": v(-72.52, 26.96) * mm, "end": v(-71.08, 25.53) * mm});
            skLineSegment(sketch, "E21.4.6.0", {"start": v(-73.95, 16.64) * mm, "end": v(-72.52, 18.07) * mm});
            skLineSegment(sketch, "E21.4.6.1", {"start": v(-72.52, 15.2) * mm, "end": v(-73.95, 16.64) * mm});
            skLineSegment(sketch, "E21.4.6.2", {"start": v(-71.08, 16.64) * mm, "end": v(-72.52, 15.2) * mm});
            skLineSegment(sketch, "E21.4.6.3", {"start": v(-72.52, 18.07) * mm, "end": v(-71.08, 16.64) * mm});
            skLineSegment(sketch, "E21.4.7.0", {"start": v(-73.95, 7.75) * mm, "end": v(-72.52, 9.18) * mm});
            skLineSegment(sketch, "E21.4.7.1", {"start": v(-72.52, 6.31) * mm, "end": v(-73.95, 7.75) * mm});
            skLineSegment(sketch, "E21.4.7.2", {"start": v(-71.08, 7.75) * mm, "end": v(-72.52, 6.31) * mm});
            skLineSegment(sketch, "E21.4.7.3", {"start": v(-72.52, 9.18) * mm, "end": v(-71.08, 7.75) * mm});
            skLineSegment(sketch, "E21.5.0.0", {"start": v(-65.06, 69.98) * mm, "end": v(-63.63, 71.41) * mm});
            skLineSegment(sketch, "E21.5.0.1", {"start": v(-63.63, 68.54) * mm, "end": v(-65.06, 69.98) * mm});
            skLineSegment(sketch, "E21.5.0.2", {"start": v(-62.2, 69.98) * mm, "end": v(-63.63, 68.54) * mm});
            skLineSegment(sketch, "E21.5.0.3", {"start": v(-63.63, 71.41) * mm, "end": v(-62.2, 69.98) * mm});
            skLineSegment(sketch, "E21.5.1.0", {"start": v(-65.06, 61.09) * mm, "end": v(-63.63, 62.52) * mm});
            skLineSegment(sketch, "E21.5.1.1", {"start": v(-63.63, 59.65) * mm, "end": v(-65.06, 61.09) * mm});
            skLineSegment(sketch, "E21.5.1.2", {"start": v(-62.2, 61.09) * mm, "end": v(-63.63, 59.65) * mm});
            skLineSegment(sketch, "E21.5.1.3", {"start": v(-63.63, 62.52) * mm, "end": v(-62.2, 61.09) * mm});
            skLineSegment(sketch, "E21.5.2.0", {"start": v(-65.06, 52.2) * mm, "end": v(-63.63, 53.63) * mm});
            skLineSegment(sketch, "E21.5.2.1", {"start": v(-63.63, 50.76) * mm, "end": v(-65.06, 52.2) * mm});
            skLineSegment(sketch, "E21.5.2.2", {"start": v(-62.2, 52.2) * mm, "end": v(-63.63, 50.76) * mm});
            skLineSegment(sketch, "E21.5.2.3", {"start": v(-63.63, 53.63) * mm, "end": v(-62.2, 52.2) * mm});
            skLineSegment(sketch, "E21.5.3.0", {"start": v(-65.06, 43.3) * mm, "end": v(-63.63, 44.74) * mm});
            skLineSegment(sketch, "E21.5.3.1", {"start": v(-63.63, 41.87) * mm, "end": v(-65.06, 43.3) * mm});
            skLineSegment(sketch, "E21.5.3.2", {"start": v(-62.2, 43.3) * mm, "end": v(-63.63, 41.87) * mm});
            skLineSegment(sketch, "E21.5.3.3", {"start": v(-63.63, 44.74) * mm, "end": v(-62.2, 43.3) * mm});
            skLineSegment(sketch, "E21.5.4.0", {"start": v(-65.06, 34.42) * mm, "end": v(-63.63, 35.85) * mm});
            skLineSegment(sketch, "E21.5.4.1", {"start": v(-63.63, 32.98) * mm, "end": v(-65.06, 34.42) * mm});
            skLineSegment(sketch, "E21.5.4.2", {"start": v(-62.2, 34.42) * mm, "end": v(-63.63, 32.98) * mm});
            skLineSegment(sketch, "E21.5.4.3", {"start": v(-63.63, 35.85) * mm, "end": v(-62.2, 34.42) * mm});
            skLineSegment(sketch, "E21.5.5.0", {"start": v(-65.06, 25.53) * mm, "end": v(-63.63, 26.96) * mm});
            skLineSegment(sketch, "E21.5.5.1", {"start": v(-63.63, 24.1) * mm, "end": v(-65.06, 25.53) * mm});
            skLineSegment(sketch, "E21.5.5.2", {"start": v(-62.2, 25.53) * mm, "end": v(-63.63, 24.1) * mm});
            skLineSegment(sketch, "E21.5.5.3", {"start": v(-63.63, 26.96) * mm, "end": v(-62.2, 25.53) * mm});
            skLineSegment(sketch, "E21.5.6.0", {"start": v(-65.06, 16.64) * mm, "end": v(-63.63, 18.07) * mm});
            skLineSegment(sketch, "E21.5.6.1", {"start": v(-63.63, 15.2) * mm, "end": v(-65.06, 16.64) * mm});
            skLineSegment(sketch, "E21.5.6.2", {"start": v(-62.2, 16.64) * mm, "end": v(-63.63, 15.2) * mm});
            skLineSegment(sketch, "E21.5.6.3", {"start": v(-63.63, 18.07) * mm, "end": v(-62.2, 16.64) * mm});
            skLineSegment(sketch, "E21.5.7.0", {"start": v(-65.06, 7.75) * mm, "end": v(-63.63, 9.18) * mm});
            skLineSegment(sketch, "E21.5.7.1", {"start": v(-63.63, 6.31) * mm, "end": v(-65.06, 7.75) * mm});
            skLineSegment(sketch, "E21.5.7.2", {"start": v(-62.2, 7.75) * mm, "end": v(-63.63, 6.31) * mm});
            skLineSegment(sketch, "E21.5.7.3", {"start": v(-63.63, 9.18) * mm, "end": v(-62.2, 7.75) * mm});
            skLineSegment(sketch, "E21.6.0.0", {"start": v(-56.17, 69.98) * mm, "end": v(-54.74, 71.41) * mm});
            skLineSegment(sketch, "E21.6.0.1", {"start": v(-54.74, 68.54) * mm, "end": v(-56.17, 69.98) * mm});
            skLineSegment(sketch, "E21.6.0.2", {"start": v(-53.3, 69.98) * mm, "end": v(-54.74, 68.54) * mm});
            skLineSegment(sketch, "E21.6.0.3", {"start": v(-54.74, 71.41) * mm, "end": v(-53.3, 69.98) * mm});
            skLineSegment(sketch, "E21.6.1.0", {"start": v(-56.17, 61.09) * mm, "end": v(-54.74, 62.52) * mm});
            skLineSegment(sketch, "E21.6.1.1", {"start": v(-54.74, 59.65) * mm, "end": v(-56.17, 61.09) * mm});
            skLineSegment(sketch, "E21.6.1.2", {"start": v(-53.3, 61.09) * mm, "end": v(-54.74, 59.65) * mm});
            skLineSegment(sketch, "E21.6.1.3", {"start": v(-54.74, 62.52) * mm, "end": v(-53.3, 61.09) * mm});
            skLineSegment(sketch, "E21.6.2.0", {"start": v(-56.17, 52.2) * mm, "end": v(-54.74, 53.63) * mm});
            skLineSegment(sketch, "E21.6.2.1", {"start": v(-54.74, 50.76) * mm, "end": v(-56.17, 52.2) * mm});
            skLineSegment(sketch, "E21.6.2.2", {"start": v(-53.3, 52.2) * mm, "end": v(-54.74, 50.76) * mm});
            skLineSegment(sketch, "E21.6.2.3", {"start": v(-54.74, 53.63) * mm, "end": v(-53.3, 52.2) * mm});
            skLineSegment(sketch, "E21.6.3.0", {"start": v(-56.17, 43.3) * mm, "end": v(-54.74, 44.74) * mm});
            skLineSegment(sketch, "E21.6.3.1", {"start": v(-54.74, 41.87) * mm, "end": v(-56.17, 43.3) * mm});
            skLineSegment(sketch, "E21.6.3.2", {"start": v(-53.3, 43.3) * mm, "end": v(-54.74, 41.87) * mm});
            skLineSegment(sketch, "E21.6.3.3", {"start": v(-54.74, 44.74) * mm, "end": v(-53.3, 43.3) * mm});
            skLineSegment(sketch, "E21.6.4.0", {"start": v(-56.17, 34.42) * mm, "end": v(-54.74, 35.85) * mm});
            skLineSegment(sketch, "E21.6.4.1", {"start": v(-54.74, 32.98) * mm, "end": v(-56.17, 34.42) * mm});
            skLineSegment(sketch, "E21.6.4.2", {"start": v(-53.3, 34.42) * mm, "end": v(-54.74, 32.98) * mm});
            skLineSegment(sketch, "E21.6.4.3", {"start": v(-54.74, 35.85) * mm, "end": v(-53.3, 34.42) * mm});
            skLineSegment(sketch, "E21.6.5.0", {"start": v(-56.17, 25.53) * mm, "end": v(-54.74, 26.96) * mm});
            skLineSegment(sketch, "E21.6.5.1", {"start": v(-54.74, 24.1) * mm, "end": v(-56.17, 25.53) * mm});
            skLineSegment(sketch, "E21.6.5.2", {"start": v(-53.3, 25.53) * mm, "end": v(-54.74, 24.1) * mm});
            skLineSegment(sketch, "E21.6.5.3", {"start": v(-54.74, 26.96) * mm, "end": v(-53.3, 25.53) * mm});
            skLineSegment(sketch, "E21.6.6.0", {"start": v(-56.17, 16.64) * mm, "end": v(-54.74, 18.07) * mm});
            skLineSegment(sketch, "E21.6.6.1", {"start": v(-54.74, 15.2) * mm, "end": v(-56.17, 16.64) * mm});
            skLineSegment(sketch, "E21.6.6.2", {"start": v(-53.3, 16.64) * mm, "end": v(-54.74, 15.2) * mm});
            skLineSegment(sketch, "E21.6.6.3", {"start": v(-54.74, 18.07) * mm, "end": v(-53.3, 16.64) * mm});
            skLineSegment(sketch, "E21.6.7.0", {"start": v(-56.17, 7.75) * mm, "end": v(-54.74, 9.18) * mm});
            skLineSegment(sketch, "E21.6.7.1", {"start": v(-54.74, 6.31) * mm, "end": v(-56.17, 7.75) * mm});
            skLineSegment(sketch, "E21.6.7.2", {"start": v(-53.3, 7.75) * mm, "end": v(-54.74, 6.31) * mm});
            skLineSegment(sketch, "E21.6.7.3", {"start": v(-54.74, 9.18) * mm, "end": v(-53.3, 7.75) * mm});
            skLineSegment(sketch, "E21.7.0.0", {"start": v(-47.28, 69.98) * mm, "end": v(-45.85, 71.41) * mm});
            skLineSegment(sketch, "E21.7.0.1", {"start": v(-45.85, 68.54) * mm, "end": v(-47.28, 69.98) * mm});
            skLineSegment(sketch, "E21.7.0.2", {"start": v(-44.41, 69.98) * mm, "end": v(-45.85, 68.54) * mm});
            skLineSegment(sketch, "E21.7.0.3", {"start": v(-45.85, 71.41) * mm, "end": v(-44.41, 69.98) * mm});
            skLineSegment(sketch, "E21.7.1.0", {"start": v(-47.28, 61.09) * mm, "end": v(-45.85, 62.52) * mm});
            skLineSegment(sketch, "E21.7.1.1", {"start": v(-45.85, 59.65) * mm, "end": v(-47.28, 61.09) * mm});
            skLineSegment(sketch, "E21.7.1.2", {"start": v(-44.41, 61.09) * mm, "end": v(-45.85, 59.65) * mm});
            skLineSegment(sketch, "E21.7.1.3", {"start": v(-45.85, 62.52) * mm, "end": v(-44.41, 61.09) * mm});
            skLineSegment(sketch, "E21.7.2.0", {"start": v(-47.28, 52.2) * mm, "end": v(-45.85, 53.63) * mm});
            skLineSegment(sketch, "E21.7.2.1", {"start": v(-45.85, 50.76) * mm, "end": v(-47.28, 52.2) * mm});
            skLineSegment(sketch, "E21.7.2.2", {"start": v(-44.41, 52.2) * mm, "end": v(-45.85, 50.76) * mm});
            skLineSegment(sketch, "E21.7.2.3", {"start": v(-45.85, 53.63) * mm, "end": v(-44.41, 52.2) * mm});
            skLineSegment(sketch, "E21.7.3.0", {"start": v(-47.28, 43.3) * mm, "end": v(-45.85, 44.74) * mm});
            skLineSegment(sketch, "E21.7.3.1", {"start": v(-45.85, 41.87) * mm, "end": v(-47.28, 43.3) * mm});
            skLineSegment(sketch, "E21.7.3.2", {"start": v(-44.41, 43.3) * mm, "end": v(-45.85, 41.87) * mm});
            skLineSegment(sketch, "E21.7.3.3", {"start": v(-45.85, 44.74) * mm, "end": v(-44.41, 43.3) * mm});
            skLineSegment(sketch, "E21.7.4.0", {"start": v(-47.28, 34.42) * mm, "end": v(-45.85, 35.85) * mm});
            skLineSegment(sketch, "E21.7.4.1", {"start": v(-45.85, 32.98) * mm, "end": v(-47.28, 34.42) * mm});
            skLineSegment(sketch, "E21.7.4.2", {"start": v(-44.41, 34.42) * mm, "end": v(-45.85, 32.98) * mm});
            skLineSegment(sketch, "E21.7.4.3", {"start": v(-45.85, 35.85) * mm, "end": v(-44.41, 34.42) * mm});
            skLineSegment(sketch, "E21.7.5.0", {"start": v(-47.28, 25.53) * mm, "end": v(-45.85, 26.96) * mm});
            skLineSegment(sketch, "E21.7.5.1", {"start": v(-45.85, 24.1) * mm, "end": v(-47.28, 25.53) * mm});
            skLineSegment(sketch, "E21.7.5.2", {"start": v(-44.41, 25.53) * mm, "end": v(-45.85, 24.1) * mm});
            skLineSegment(sketch, "E21.7.5.3", {"start": v(-45.85, 26.96) * mm, "end": v(-44.41, 25.53) * mm});
            skLineSegment(sketch, "E21.7.6.0", {"start": v(-47.28, 16.64) * mm, "end": v(-45.85, 18.07) * mm});
            skLineSegment(sketch, "E21.7.6.1", {"start": v(-45.85, 15.2) * mm, "end": v(-47.28, 16.64) * mm});
            skLineSegment(sketch, "E21.7.6.2", {"start": v(-44.41, 16.64) * mm, "end": v(-45.85, 15.2) * mm});
            skLineSegment(sketch, "E21.7.6.3", {"start": v(-45.85, 18.07) * mm, "end": v(-44.41, 16.64) * mm});
            skLineSegment(sketch, "E21.7.7.0", {"start": v(-47.28, 7.75) * mm, "end": v(-45.85, 9.18) * mm});
            skLineSegment(sketch, "E21.7.7.1", {"start": v(-45.85, 6.31) * mm, "end": v(-47.28, 7.75) * mm});
            skLineSegment(sketch, "E21.7.7.2", {"start": v(-44.41, 7.75) * mm, "end": v(-45.85, 6.31) * mm});
            skLineSegment(sketch, "E21.7.7.3", {"start": v(-45.85, 9.18) * mm, "end": v(-44.41, 7.75) * mm});
            skLineSegment(sketch, "E21.8.0.0", {"start": v(-38.4, 69.98) * mm, "end": v(-36.96, 71.41) * mm});
            skLineSegment(sketch, "E21.8.0.1", {"start": v(-36.96, 68.54) * mm, "end": v(-38.4, 69.98) * mm});
            skLineSegment(sketch, "E21.8.0.2", {"start": v(-35.52, 69.98) * mm, "end": v(-36.96, 68.54) * mm});
            skLineSegment(sketch, "E21.8.0.3", {"start": v(-36.96, 71.41) * mm, "end": v(-35.52, 69.98) * mm});
            skLineSegment(sketch, "E21.8.1.0", {"start": v(-38.4, 61.09) * mm, "end": v(-36.96, 62.52) * mm});
            skLineSegment(sketch, "E21.8.1.1", {"start": v(-36.96, 59.65) * mm, "end": v(-38.4, 61.09) * mm});
            skLineSegment(sketch, "E21.8.1.2", {"start": v(-35.52, 61.09) * mm, "end": v(-36.96, 59.65) * mm});
            skLineSegment(sketch, "E21.8.1.3", {"start": v(-36.96, 62.52) * mm, "end": v(-35.52, 61.09) * mm});
            skLineSegment(sketch, "E21.8.2.0", {"start": v(-38.4, 52.2) * mm, "end": v(-36.96, 53.63) * mm});
            skLineSegment(sketch, "E21.8.2.1", {"start": v(-36.96, 50.76) * mm, "end": v(-38.4, 52.2) * mm});
            skLineSegment(sketch, "E21.8.2.2", {"start": v(-35.52, 52.2) * mm, "end": v(-36.96, 50.76) * mm});
            skLineSegment(sketch, "E21.8.2.3", {"start": v(-36.96, 53.63) * mm, "end": v(-35.52, 52.2) * mm});
            skLineSegment(sketch, "E21.8.3.0", {"start": v(-38.4, 43.3) * mm, "end": v(-36.96, 44.74) * mm});
            skLineSegment(sketch, "E21.8.3.1", {"start": v(-36.96, 41.87) * mm, "end": v(-38.4, 43.3) * mm});
            skLineSegment(sketch, "E21.8.3.2", {"start": v(-35.52, 43.3) * mm, "end": v(-36.96, 41.87) * mm});
            skLineSegment(sketch, "E21.8.3.3", {"start": v(-36.96, 44.74) * mm, "end": v(-35.52, 43.3) * mm});
            skLineSegment(sketch, "E21.8.4.0", {"start": v(-38.4, 34.42) * mm, "end": v(-36.96, 35.85) * mm});
            skLineSegment(sketch, "E21.8.4.1", {"start": v(-36.96, 32.98) * mm, "end": v(-38.4, 34.42) * mm});
            skLineSegment(sketch, "E21.8.4.2", {"start": v(-35.52, 34.42) * mm, "end": v(-36.96, 32.98) * mm});
            skLineSegment(sketch, "E21.8.4.3", {"start": v(-36.96, 35.85) * mm, "end": v(-35.52, 34.42) * mm});
            skLineSegment(sketch, "E21.8.5.0", {"start": v(-38.4, 25.53) * mm, "end": v(-36.96, 26.96) * mm});
            skLineSegment(sketch, "E21.8.5.1", {"start": v(-36.96, 24.1) * mm, "end": v(-38.4, 25.53) * mm});
            skLineSegment(sketch, "E21.8.5.2", {"start": v(-35.52, 25.53) * mm, "end": v(-36.96, 24.1) * mm});
            skLineSegment(sketch, "E21.8.5.3", {"start": v(-36.96, 26.96) * mm, "end": v(-35.52, 25.53) * mm});
            skLineSegment(sketch, "E21.8.6.0", {"start": v(-38.4, 16.64) * mm, "end": v(-36.96, 18.07) * mm});
            skLineSegment(sketch, "E21.8.6.1", {"start": v(-36.96, 15.2) * mm, "end": v(-38.4, 16.64) * mm});
            skLineSegment(sketch, "E21.8.6.2", {"start": v(-35.52, 16.64) * mm, "end": v(-36.96, 15.2) * mm});
            skLineSegment(sketch, "E21.8.6.3", {"start": v(-36.96, 18.07) * mm, "end": v(-35.52, 16.64) * mm});
            skLineSegment(sketch, "E21.8.7.0", {"start": v(-38.4, 7.75) * mm, "end": v(-36.96, 9.18) * mm});
            skLineSegment(sketch, "E21.8.7.1", {"start": v(-36.96, 6.31) * mm, "end": v(-38.4, 7.75) * mm});
            skLineSegment(sketch, "E21.8.7.2", {"start": v(-35.52, 7.75) * mm, "end": v(-36.96, 6.31) * mm});
            skLineSegment(sketch, "E21.8.7.3", {"start": v(-36.96, 9.18) * mm, "end": v(-35.52, 7.75) * mm});
            skLineSegment(sketch, "E21.9.0.0", {"start": v(-29.5, 69.98) * mm, "end": v(-28.07, 71.41) * mm});
            skLineSegment(sketch, "E21.9.0.1", {"start": v(-28.07, 68.54) * mm, "end": v(-29.5, 69.98) * mm});
            skLineSegment(sketch, "E21.9.0.2", {"start": v(-26.63, 69.98) * mm, "end": v(-28.07, 68.54) * mm});
            skLineSegment(sketch, "E21.9.0.3", {"start": v(-28.07, 71.41) * mm, "end": v(-26.63, 69.98) * mm});
            skLineSegment(sketch, "E21.9.1.0", {"start": v(-29.5, 61.09) * mm, "end": v(-28.07, 62.52) * mm});
            skLineSegment(sketch, "E21.9.1.1", {"start": v(-28.07, 59.65) * mm, "end": v(-29.5, 61.09) * mm});
            skLineSegment(sketch, "E21.9.1.2", {"start": v(-26.63, 61.09) * mm, "end": v(-28.07, 59.65) * mm});
            skLineSegment(sketch, "E21.9.1.3", {"start": v(-28.07, 62.52) * mm, "end": v(-26.63, 61.09) * mm});
            skLineSegment(sketch, "E21.9.2.0", {"start": v(-29.5, 52.2) * mm, "end": v(-28.07, 53.63) * mm});
            skLineSegment(sketch, "E21.9.2.1", {"start": v(-28.07, 50.76) * mm, "end": v(-29.5, 52.2) * mm});
            skLineSegment(sketch, "E21.9.2.2", {"start": v(-26.63, 52.2) * mm, "end": v(-28.07, 50.76) * mm});
            skLineSegment(sketch, "E21.9.2.3", {"start": v(-28.07, 53.63) * mm, "end": v(-26.63, 52.2) * mm});
            skLineSegment(sketch, "E21.9.3.0", {"start": v(-29.5, 43.3) * mm, "end": v(-28.07, 44.74) * mm});
            skLineSegment(sketch, "E21.9.3.1", {"start": v(-28.07, 41.87) * mm, "end": v(-29.5, 43.3) * mm});
            skLineSegment(sketch, "E21.9.3.2", {"start": v(-26.63, 43.3) * mm, "end": v(-28.07, 41.87) * mm});
            skLineSegment(sketch, "E21.9.3.3", {"start": v(-28.07, 44.74) * mm, "end": v(-26.63, 43.3) * mm});
            skLineSegment(sketch, "E21.9.4.0", {"start": v(-29.5, 34.42) * mm, "end": v(-28.07, 35.85) * mm});
            skLineSegment(sketch, "E21.9.4.1", {"start": v(-28.07, 32.98) * mm, "end": v(-29.5, 34.42) * mm});
            skLineSegment(sketch, "E21.9.4.2", {"start": v(-26.63, 34.42) * mm, "end": v(-28.07, 32.98) * mm});
            skLineSegment(sketch, "E21.9.4.3", {"start": v(-28.07, 35.85) * mm, "end": v(-26.63, 34.42) * mm});
            skLineSegment(sketch, "E21.9.5.0", {"start": v(-29.5, 25.53) * mm, "end": v(-28.07, 26.96) * mm});
            skLineSegment(sketch, "E21.9.5.1", {"start": v(-28.07, 24.1) * mm, "end": v(-29.5, 25.53) * mm});
            skLineSegment(sketch, "E21.9.5.2", {"start": v(-26.63, 25.53) * mm, "end": v(-28.07, 24.1) * mm});
            skLineSegment(sketch, "E21.9.5.3", {"start": v(-28.07, 26.96) * mm, "end": v(-26.63, 25.53) * mm});
            skLineSegment(sketch, "E21.9.6.0", {"start": v(-29.5, 16.64) * mm, "end": v(-28.07, 18.07) * mm});
            skLineSegment(sketch, "E21.9.6.1", {"start": v(-28.07, 15.2) * mm, "end": v(-29.5, 16.64) * mm});
            skLineSegment(sketch, "E21.9.6.2", {"start": v(-26.63, 16.64) * mm, "end": v(-28.07, 15.2) * mm});
            skLineSegment(sketch, "E21.9.6.3", {"start": v(-28.07, 18.07) * mm, "end": v(-26.63, 16.64) * mm});
            skLineSegment(sketch, "E21.9.7.0", {"start": v(-29.5, 7.75) * mm, "end": v(-28.07, 9.18) * mm});
            skLineSegment(sketch, "E21.9.7.1", {"start": v(-28.07, 6.31) * mm, "end": v(-29.5, 7.75) * mm});
            skLineSegment(sketch, "E21.9.7.2", {"start": v(-26.63, 7.75) * mm, "end": v(-28.07, 6.31) * mm});
            skLineSegment(sketch, "E21.9.7.3", {"start": v(-28.07, 9.18) * mm, "end": v(-26.63, 7.75) * mm});
            skLineSegment(sketch, "E21.10.0.0", {"start": v(-20.61, 69.98) * mm, "end": v(-19.18, 71.41) * mm});
            skLineSegment(sketch, "E21.10.0.1", {"start": v(-19.18, 68.54) * mm, "end": v(-20.61, 69.98) * mm});
            skLineSegment(sketch, "E21.10.0.2", {"start": v(-17.74, 69.98) * mm, "end": v(-19.18, 68.54) * mm});
            skLineSegment(sketch, "E21.10.0.3", {"start": v(-19.18, 71.41) * mm, "end": v(-17.74, 69.98) * mm});
            skLineSegment(sketch, "E21.10.1.0", {"start": v(-20.61, 61.09) * mm, "end": v(-19.18, 62.52) * mm});
            skLineSegment(sketch, "E21.10.1.1", {"start": v(-19.18, 59.65) * mm, "end": v(-20.61, 61.09) * mm});
            skLineSegment(sketch, "E21.10.1.2", {"start": v(-17.74, 61.09) * mm, "end": v(-19.18, 59.65) * mm});
            skLineSegment(sketch, "E21.10.1.3", {"start": v(-19.18, 62.52) * mm, "end": v(-17.74, 61.09) * mm});
            skLineSegment(sketch, "E21.10.2.0", {"start": v(-20.61, 52.2) * mm, "end": v(-19.18, 53.63) * mm});
            skLineSegment(sketch, "E21.10.2.1", {"start": v(-19.18, 50.76) * mm, "end": v(-20.61, 52.2) * mm});
            skLineSegment(sketch, "E21.10.2.2", {"start": v(-17.74, 52.2) * mm, "end": v(-19.18, 50.76) * mm});
            skLineSegment(sketch, "E21.10.2.3", {"start": v(-19.18, 53.63) * mm, "end": v(-17.74, 52.2) * mm});
            skLineSegment(sketch, "E21.10.3.0", {"start": v(-20.61, 43.3) * mm, "end": v(-19.18, 44.74) * mm});
            skLineSegment(sketch, "E21.10.3.1", {"start": v(-19.18, 41.87) * mm, "end": v(-20.61, 43.3) * mm});
            skLineSegment(sketch, "E21.10.3.2", {"start": v(-17.74, 43.3) * mm, "end": v(-19.18, 41.87) * mm});
            skLineSegment(sketch, "E21.10.3.3", {"start": v(-19.18, 44.74) * mm, "end": v(-17.74, 43.3) * mm});
            skLineSegment(sketch, "E21.10.4.0", {"start": v(-20.61, 34.42) * mm, "end": v(-19.18, 35.85) * mm});
            skLineSegment(sketch, "E21.10.4.1", {"start": v(-19.18, 32.98) * mm, "end": v(-20.61, 34.42) * mm});
            skLineSegment(sketch, "E21.10.4.2", {"start": v(-17.74, 34.42) * mm, "end": v(-19.18, 32.98) * mm});
            skLineSegment(sketch, "E21.10.4.3", {"start": v(-19.18, 35.85) * mm, "end": v(-17.74, 34.42) * mm});
            skLineSegment(sketch, "E21.10.5.0", {"start": v(-20.61, 25.53) * mm, "end": v(-19.18, 26.96) * mm});
            skLineSegment(sketch, "E21.10.5.1", {"start": v(-19.18, 24.1) * mm, "end": v(-20.61, 25.53) * mm});
            skLineSegment(sketch, "E21.10.5.2", {"start": v(-17.74, 25.53) * mm, "end": v(-19.18, 24.1) * mm});
            skLineSegment(sketch, "E21.10.5.3", {"start": v(-19.18, 26.96) * mm, "end": v(-17.74, 25.53) * mm});
            skLineSegment(sketch, "E21.10.6.0", {"start": v(-20.61, 16.64) * mm, "end": v(-19.18, 18.07) * mm});
            skLineSegment(sketch, "E21.10.6.1", {"start": v(-19.18, 15.2) * mm, "end": v(-20.61, 16.64) * mm});
            skLineSegment(sketch, "E21.10.6.2", {"start": v(-17.74, 16.64) * mm, "end": v(-19.18, 15.2) * mm});
            skLineSegment(sketch, "E21.10.6.3", {"start": v(-19.18, 18.07) * mm, "end": v(-17.74, 16.64) * mm});
            skLineSegment(sketch, "E21.10.7.0", {"start": v(-20.61, 7.75) * mm, "end": v(-19.18, 9.18) * mm});
            skLineSegment(sketch, "E21.10.7.1", {"start": v(-19.18, 6.31) * mm, "end": v(-20.61, 7.75) * mm});
            skLineSegment(sketch, "E21.10.7.2", {"start": v(-17.74, 7.75) * mm, "end": v(-19.18, 6.31) * mm});
            skLineSegment(sketch, "E21.10.7.3", {"start": v(-19.18, 9.18) * mm, "end": v(-17.74, 7.75) * mm});
            skLineSegment(sketch, "E21.11.0.0", {"start": v(-11.72, 69.98) * mm, "end": v(-10.29, 71.41) * mm});
            skLineSegment(sketch, "E21.11.0.1", {"start": v(-10.29, 68.54) * mm, "end": v(-11.72, 69.98) * mm});
            skLineSegment(sketch, "E21.11.0.2", {"start": v(-8.85, 69.98) * mm, "end": v(-10.29, 68.54) * mm});
            skLineSegment(sketch, "E21.11.0.3", {"start": v(-10.29, 71.41) * mm, "end": v(-8.85, 69.98) * mm});
            skLineSegment(sketch, "E21.11.1.0", {"start": v(-11.72, 61.09) * mm, "end": v(-10.29, 62.52) * mm});
            skLineSegment(sketch, "E21.11.1.1", {"start": v(-10.29, 59.65) * mm, "end": v(-11.72, 61.09) * mm});
            skLineSegment(sketch, "E21.11.1.2", {"start": v(-8.85, 61.09) * mm, "end": v(-10.29, 59.65) * mm});
            skLineSegment(sketch, "E21.11.1.3", {"start": v(-10.29, 62.52) * mm, "end": v(-8.85, 61.09) * mm});
            skLineSegment(sketch, "E21.11.2.0", {"start": v(-11.72, 52.2) * mm, "end": v(-10.29, 53.63) * mm});
            skLineSegment(sketch, "E21.11.2.1", {"start": v(-10.29, 50.76) * mm, "end": v(-11.72, 52.2) * mm});
            skLineSegment(sketch, "E21.11.2.2", {"start": v(-8.85, 52.2) * mm, "end": v(-10.29, 50.76) * mm});
            skLineSegment(sketch, "E21.11.2.3", {"start": v(-10.29, 53.63) * mm, "end": v(-8.85, 52.2) * mm});
            skLineSegment(sketch, "E21.11.3.0", {"start": v(-11.72, 43.3) * mm, "end": v(-10.29, 44.74) * mm});
            skLineSegment(sketch, "E21.11.3.1", {"start": v(-10.29, 41.87) * mm, "end": v(-11.72, 43.3) * mm});
            skLineSegment(sketch, "E21.11.3.2", {"start": v(-8.85, 43.3) * mm, "end": v(-10.29, 41.87) * mm});
            skLineSegment(sketch, "E21.11.3.3", {"start": v(-10.29, 44.74) * mm, "end": v(-8.85, 43.3) * mm});
            skLineSegment(sketch, "E21.11.4.0", {"start": v(-11.72, 34.42) * mm, "end": v(-10.29, 35.85) * mm});
            skLineSegment(sketch, "E21.11.4.1", {"start": v(-10.29, 32.98) * mm, "end": v(-11.72, 34.42) * mm});
            skLineSegment(sketch, "E21.11.4.2", {"start": v(-8.85, 34.42) * mm, "end": v(-10.29, 32.98) * mm});
            skLineSegment(sketch, "E21.11.4.3", {"start": v(-10.29, 35.85) * mm, "end": v(-8.85, 34.42) * mm});
            skLineSegment(sketch, "E21.11.5.0", {"start": v(-11.72, 25.53) * mm, "end": v(-10.29, 26.96) * mm});
            skLineSegment(sketch, "E21.11.5.1", {"start": v(-10.29, 24.1) * mm, "end": v(-11.72, 25.53) * mm});
            skLineSegment(sketch, "E21.11.5.2", {"start": v(-8.85, 25.53) * mm, "end": v(-10.29, 24.1) * mm});
            skLineSegment(sketch, "E21.11.5.3", {"start": v(-10.29, 26.96) * mm, "end": v(-8.85, 25.53) * mm});
            skLineSegment(sketch, "E21.11.6.0", {"start": v(-11.72, 16.64) * mm, "end": v(-10.29, 18.07) * mm});
            skLineSegment(sketch, "E21.11.6.1", {"start": v(-10.29, 15.2) * mm, "end": v(-11.72, 16.64) * mm});
            skLineSegment(sketch, "E21.11.6.2", {"start": v(-8.85, 16.64) * mm, "end": v(-10.29, 15.2) * mm});
            skLineSegment(sketch, "E21.11.6.3", {"start": v(-10.29, 18.07) * mm, "end": v(-8.85, 16.64) * mm});
            skLineSegment(sketch, "E21.11.7.0", {"start": v(-11.72, 7.75) * mm, "end": v(-10.29, 9.18) * mm});
            skLineSegment(sketch, "E21.11.7.1", {"start": v(-10.29, 6.31) * mm, "end": v(-11.72, 7.75) * mm});
            skLineSegment(sketch, "E21.11.7.2", {"start": v(-8.85, 7.75) * mm, "end": v(-10.29, 6.31) * mm});
            skLineSegment(sketch, "E21.11.7.3", {"start": v(-10.29, 9.18) * mm, "end": v(-8.85, 7.75) * mm});
            skLineSegment(sketch, "E21.direction1", {"start": v(-108.08, 68.54) * mm, "end": v(-99.19, 68.54) * mm, "construction": true});
            skLineSegment(sketch, "E21.direction2", {"start": v(-108.08, 68.54) * mm, "end": v(-108.08, 59.65) * mm, "construction": true});
            skSolve(sketch);
        }
        {
            var Q0;
            Q0 = qSketchRegion(id + "F2", true);
            extrude(context, id + "F5", {"entities" : qUnion([Q0]), "operationType" : NewBodyOperationType.ADD, "oppositeDirection" : true, "depth" : 4 * mm});
        }
        {
            var Q0;
            Q0 = qSketchRegion(id + "F4", true);
            extrude(context, id + "F6", {"entities" : qUnion([Q0]), "depth" : 1 * mm});
        }
        {
            var Q0;
            Q0=makeQuery(id+"F5.opExtrude","CAP_FACE",FACE,{"disambiguationData":[OSD([sQuery(id+"F2.wireOp",EDGE,"E6"),sQuery(id+"F2.wireOp",EDGE,"E7"),sQuery(id+"F2.wireOp",EDGE,"E8"),sQuery(id+"F2.wireOp",EDGE,"E9")])],"isStart":false});
            var Q1;
            Q1=makeQuery(id+"F6.opExtrude","CAP_FACE",FACE,{"disambiguationData":[OSD([sQuery(id+"F4.wireOp",EDGE,"E15"),sQuery(id+"F4.wireOp",EDGE,"E16"),sQuery(id+"F4.wireOp",EDGE,"E17"),sQuery(id+"F4.wireOp",EDGE,"E18")])],"isStart":true});
            loft(context, id + "F7", {"operationType" : NewBodyOperationType.ADD, "endCondition" : LoftEndDerivativeType.MATCH_CURVATURE, "endMagnitude" : 1, "sheetProfilesArray" : [{ "sheetProfileEntities" : qUnion([Q0]) }, { "sheetProfileEntities" : qUnion([Q1]) }]});
        }
        {
            var Q0;
            Q0=makeQuery(id+"F5.opExtrude","CAP_FACE",FACE,{"disambiguationData":[OSD([sQuery(id+"F2.wireOp",EDGE,"E14.0.1.0"),sQuery(id+"F2.wireOp",EDGE,"E14.0.1.1"),sQuery(id+"F2.wireOp",EDGE,"E14.0.1.2"),sQuery(id+"F2.wireOp",EDGE,"E14.0.1.3")])],"isStart":false});
            var Q1;
            Q1=makeQuery(id+"F6.opExtrude","CAP_FACE",FACE,{"disambiguationData":[OSD([sQuery(id+"F4.wireOp",EDGE,"E21.0.1.0"),sQuery(id+"F4.wireOp",EDGE,"E21.0.1.1"),sQuery(id+"F4.wireOp",EDGE,"E21.0.1.2"),sQuery(id+"F4.wireOp",EDGE,"E21.0.1.3")])],"isStart":true});
            loft(context, id + "F8", {"operationType" : NewBodyOperationType.ADD, "startCondition" : LoftEndDerivativeType.MATCH_TANGENT, "startMagnitude" : 1, "sheetProfilesArray" : [{ "sheetProfileEntities" : qUnion([Q0]) }, { "sheetProfileEntities" : qUnion([Q1]) }]});
        }
        {
            var Q0;
            Q0=makeQuery(id+"F5.opExtrude","CAP_FACE",FACE,{"disambiguationData":[OSD([sQuery(id+"F2.wireOp",EDGE,"E14.1.1.0"),sQuery(id+"F2.wireOp",EDGE,"E14.1.1.1"),sQuery(id+"F2.wireOp",EDGE,"E14.1.1.2"),sQuery(id+"F2.wireOp",EDGE,"E14.1.1.3")])],"isStart":false});
            var Q1;
            Q1=makeQuery(id+"F6.opExtrude","CAP_FACE",FACE,{"disambiguationData":[OSD([sQuery(id+"F4.wireOp",EDGE,"E21.1.1.0"),sQuery(id+"F4.wireOp",EDGE,"E21.1.1.1"),sQuery(id+"F4.wireOp",EDGE,"E21.1.1.2"),sQuery(id+"F4.wireOp",EDGE,"E21.1.1.3")])],"isStart":false});
            loft(context, id + "F9", {"operationType" : NewBodyOperationType.ADD, "sheetProfilesArray" : [{ "sheetProfileEntities" : qUnion([Q0]) }, { "sheetProfileEntities" : qUnion([Q1]) }]});
        }
        {
            var Q0;
            Q0=makeQuery(id+"F5.opExtrude","CAP_FACE",FACE,{"disambiguationData":[OSD([sQuery(id+"F2.wireOp",EDGE,"E14.1.0.0"),sQuery(id+"F2.wireOp",EDGE,"E14.1.0.1"),sQuery(id+"F2.wireOp",EDGE,"E14.1.0.2"),sQuery(id+"F2.wireOp",EDGE,"E14.1.0.3")])],"isStart":false});
            var Q1;
            Q1=makeQuery(id+"F6.opExtrude","CAP_FACE",FACE,{"disambiguationData":[OSD([sQuery(id+"F4.wireOp",EDGE,"E21.1.0.0"),sQuery(id+"F4.wireOp",EDGE,"E21.1.0.1"),sQuery(id+"F4.wireOp",EDGE,"E21.1.0.2"),sQuery(id+"F4.wireOp",EDGE,"E21.1.0.3")])],"isStart":false});
            loft(context, id + "F10", {"operationType" : NewBodyOperationType.ADD, "startCondition" : LoftEndDerivativeType.NORMAL_TO_PROFILE, "startMagnitude" : 1, "endCondition" : LoftEndDerivativeType.NORMAL_TO_PROFILE, "endMagnitude" : 1, "sheetProfilesArray" : [{ "sheetProfileEntities" : qUnion([Q0]) }, { "sheetProfileEntities" : qUnion([Q1]) }]});
        }
    });
